FCSTD DOCUMENT  (FreeCAD 0.22R38314 (Git))
Label: myFile.groovy
License: All rights reserved
LicenseURL: https://en.wikipedia.org/wiki/All_rights_reserved
objects: Part::Feature×4, PartDesign::Plane×4, Sketcher::SketchObject×4, Mesh::Feature×2, PartDesign::Body×1
note: 13 computed .brp shape members not serialized (recipe doc carries the construction recipe); baked Part::Feature solids carry a one-line shape summary decoded from their .brp

FEATURE [Part::Feature] ReferenceFrame
  Placement = pos=(30,0,0) rot=(0,-1,0;1.57076rad)
FEATURE [PartDesign::Plane] DatumPlane_upperArm_1
  Length = 20
  Placement = pos=(30,0,0) rot=(0,-1,0;1.57076rad)
  ResizeMode = 0
  Width = 20
FEATURE [Sketcher::SketchObject] SVGSketch_upperArm_1
  FullyConstrained = false
  Placement = pos=(30,0,0) rot=(0,-1,0;1.57076rad)
  sketch-geometry (137):
    g0: LineSegment StartX=2.496 StartY=2.988 StartZ=0 EndX=2.388 EndY=2.988 EndZ=0
    g1: LineSegment StartX=2.388 StartY=2.988 StartZ=0 EndX=2.28 EndY=2.964 EndZ=0
    g2: LineSegment StartX=2.28 StartY=2.964 StartZ=0 EndX=2.172 EndY=2.952 EndZ=0
    g3: LineSegment StartX=2.172 StartY=2.952 StartZ=0 EndX=2.064 EndY=2.922 EndZ=0
    g4: LineSegment StartX=2.064 StartY=2.922 StartZ=0 EndX=1.962 EndY=2.892 EndZ=0
    g5: LineSegment StartX=1.962 StartY=2.892 StartZ=0 EndX=1.86 EndY=2.85 EndZ=0
    g6: LineSegment StartX=1.86 StartY=2.85 StartZ=0 EndX=1.764 EndY=2.808 EndZ=0
    g7: LineSegment StartX=1.764 StartY=2.808 StartZ=0 EndX=1.662 EndY=2.754 EndZ=0
    g8: LineSegment StartX=1.662 StartY=2.754 StartZ=0 EndX=1.59 EndY=2.718 EndZ=0
    g9: LineSegment StartX=1.59 StartY=2.718 StartZ=0 EndX=1.5 EndY=2.658 EndZ=0
    g10: LineSegment StartX=1.5 StartY=2.658 StartZ=0 EndX=1.392 EndY=2.586 EndZ=0
    g11: LineSegment StartX=1.392 StartY=2.586 StartZ=0 EndX=1.308 EndY=2.514 EndZ=0
    g12: LineSegment StartX=1.308 StartY=2.514 StartZ=0 EndX=1.224 EndY=2.442 EndZ=0
    g13: LineSegment StartX=1.224 StartY=2.442 StartZ=0 EndX=1.152 EndY=2.364 EndZ=0
    g14: LineSegment StartX=1.152 StartY=2.364 StartZ=0 EndX=1.074 EndY=2.28 EndZ=0
    g15: LineSegment StartX=1.074 StartY=2.28 StartZ=0 EndX=0.96 EndY=2.142 EndZ=0
    g16: LineSegment StartX=0.96 StartY=2.142 StartZ=0 EndX=0.804 EndY=1.956 EndZ=0
    g17: LineSegment StartX=0.804 StartY=1.956 StartZ=0 EndX=0.762 EndY=1.908 EndZ=0
    g18: LineSegment StartX=0.762 StartY=1.908 StartZ=0 EndX=0.582 EndY=1.692 EndZ=0
    g19: LineSegment StartX=0.582 StartY=1.692 StartZ=0 EndX=0.468 EndY=1.56 EndZ=0
    g20: LineSegment StartX=0.468 StartY=1.56 StartZ=0 EndX=0.42 EndY=1.5 EndZ=0
    g21: LineSegment StartX=0.42 StartY=1.5 StartZ=0 EndX=0.234 EndY=1.278 EndZ=0
    g22: LineSegment StartX=0.234 StartY=1.278 StartZ=0 EndX=0.156 EndY=1.182 EndZ=0
    g23: LineSegment StartX=0.156 StartY=1.182 StartZ=0 EndX=0.138 EndY=1.164 EndZ=0
    g24: LineSegment StartX=0.138 StartY=1.164 StartZ=0 EndX=-3.6e-15 EndY=0.996 EndZ=0
    g25: LineSegment StartX=-3.6e-15 StartY=0.996 StartZ=0 EndX=-3.6e-15 EndY=0.018 EndZ=0
    g26: LineSegment StartX=-3.6e-15 StartY=0.018 StartZ=0 EndX=-3.6e-15 EndY=-1.002 EndZ=0
    g27: LineSegment StartX=-3.6e-15 StartY=-1.002 StartZ=0 EndX=0.09 EndY=-1.11 EndZ=0
    g28: LineSegment StartX=0.09 StartY=-1.11 StartZ=0 EndX=0.156 EndY=-1.194 EndZ=0
    g29: LineSegment StartX=0.156 StartY=-1.194 StartZ=0 EndX=0.234 EndY=-1.284 EndZ=0
    g30: LineSegment StartX=0.234 StartY=-1.284 StartZ=0 EndX=0.396 EndY=-1.482 EndZ=0
    g31: LineSegment StartX=0.396 StartY=-1.482 StartZ=0 EndX=0.582 EndY=-1.698 EndZ=0
    g32: LineSegment StartX=0.582 StartY=-1.698 StartZ=0 EndX=0.762 EndY=-1.914 EndZ=0
    g33: LineSegment StartX=0.762 StartY=-1.914 StartZ=0 EndX=0.804 EndY=-1.962 EndZ=0
    g34: LineSegment StartX=0.804 StartY=-1.962 StartZ=0 EndX=0.96 EndY=-2.154 EndZ=0
    g35: LineSegment StartX=0.96 StartY=-2.154 StartZ=0 EndX=1.074 EndY=-2.286 EndZ=0
    g36: LineSegment StartX=1.074 StartY=-2.286 StartZ=0 EndX=1.152 EndY=-2.37 EndZ=0
    g37: LineSegment StartX=1.152 StartY=-2.37 StartZ=0 EndX=1.224 EndY=-2.448 EndZ=0
    g38: LineSegment StartX=1.224 StartY=-2.448 StartZ=0 EndX=1.308 EndY=-2.52 EndZ=0
    g39: LineSegment StartX=1.308 StartY=-2.52 StartZ=0 EndX=1.38 EndY=-2.58 EndZ=0
    g40: LineSegment StartX=1.38 StartY=-2.58 StartZ=0 EndX=1.5 EndY=-2.664 EndZ=0
    g41: LineSegment StartX=1.5 StartY=-2.664 StartZ=0 EndX=1.59 EndY=-2.724 EndZ=0
    g42: LineSegment StartX=1.59 StartY=-2.724 StartZ=0 EndX=1.662 EndY=-2.76 EndZ=0
    g43: LineSegment StartX=1.662 StartY=-2.76 StartZ=0 EndX=1.764 EndY=-2.814 EndZ=0
    g44: LineSegment StartX=1.764 StartY=-2.814 StartZ=0 EndX=1.86 EndY=-2.856 EndZ=0
    g45: LineSegment StartX=1.86 StartY=-2.856 StartZ=0 EndX=1.962 EndY=-2.898 EndZ=0
    g46: LineSegment StartX=1.962 StartY=-2.898 StartZ=0 EndX=2.064 EndY=-2.928 EndZ=0
    g47: LineSegment StartX=2.064 StartY=-2.928 StartZ=0 EndX=2.172 EndY=-2.958 EndZ=0
    g48: LineSegment StartX=2.172 StartY=-2.958 StartZ=0 EndX=2.28 EndY=-2.97 EndZ=0
    g49: LineSegment StartX=2.28 StartY=-2.97 StartZ=0 EndX=2.388 EndY=-2.994 EndZ=0
    g50: LineSegment StartX=2.388 StartY=-2.994 StartZ=0 EndX=2.496 EndY=-2.994 EndZ=0
    g51: LineSegment StartX=2.496 StartY=-2.994 StartZ=0 EndX=2.61 EndY=-3 EndZ=0
    g52: LineSegment StartX=2.61 StartY=-3 StartZ=0 EndX=2.796 EndY=-3 EndZ=0
    g53: LineSegment StartX=2.796 StartY=-3 StartZ=0 EndX=3 EndY=-3 EndZ=0
    g54: LineSegment StartX=3 StartY=-3 StartZ=0 EndX=3.15 EndY=-2.994 EndZ=0
    g55: LineSegment StartX=3.15 StartY=-2.994 StartZ=0 EndX=3.294 EndY=-2.988 EndZ=0
    g56: LineSegment StartX=3.294 StartY=-2.988 StartZ=0 EndX=3.444 EndY=-2.964 EndZ=0
    g57: LineSegment StartX=3.444 StartY=-2.964 StartZ=0 EndX=3.582 EndY=-2.946 EndZ=0
    g58: LineSegment StartX=3.582 StartY=-2.946 StartZ=0 EndX=3.726 EndY=-2.91 EndZ=0
    g59: LineSegment StartX=3.726 StartY=-2.91 StartZ=0 EndX=3.87 EndY=-2.874 EndZ=0
    g60: LineSegment StartX=3.87 StartY=-2.874 StartZ=0 EndX=4.008 EndY=-2.82 EndZ=0
    g61: LineSegment StartX=4.008 StartY=-2.82 StartZ=0 EndX=4.146 EndY=-2.772 EndZ=0
    g62: LineSegment StartX=4.146 StartY=-2.772 StartZ=0 EndX=4.284 EndY=-2.712 EndZ=0
    g63: LineSegment StartX=4.284 StartY=-2.712 StartZ=0 EndX=4.32 EndY=-2.694 EndZ=0
    g64: LineSegment StartX=4.32 StartY=-2.694 StartZ=0 EndX=4.446 EndY=-2.616 EndZ=0
    g65: LineSegment StartX=4.446 StartY=-2.616 StartZ=0 EndX=4.56 EndY=-2.562 EndZ=0
    g66: LineSegment StartX=4.56 StartY=-2.562 StartZ=0 EndX=4.662 EndY=-2.496 EndZ=0
    g67: LineSegment StartX=4.662 StartY=-2.496 StartZ=0 EndX=4.758 EndY=-2.43 EndZ=0
    g68: LineSegment StartX=4.758 StartY=-2.43 StartZ=0 EndX=4.854 EndY=-2.34 EndZ=0
    g69: LineSegment StartX=4.854 StartY=-2.34 StartZ=0 EndX=4.938 EndY=-2.28 EndZ=0
    g70: LineSegment StartX=4.938 StartY=-2.28 StartZ=0 EndX=4.974 EndY=-2.256 EndZ=0
    g71: LineSegment StartX=4.974 StartY=-2.256 StartZ=0 EndX=5.01 EndY=-2.22 EndZ=0
    g72: LineSegment StartX=5.01 StartY=-2.22 StartZ=0 EndX=5.118 EndY=-2.124 EndZ=0
    g73: LineSegment StartX=5.118 StartY=-2.124 StartZ=0 EndX=5.22 EndY=-2.016 EndZ=0
    g74: LineSegment StartX=5.22 StartY=-2.016 StartZ=0 EndX=5.31 EndY=-1.89 EndZ=0
    g75: LineSegment StartX=5.31 StartY=-1.89 StartZ=0 EndX=5.364 EndY=-1.836 EndZ=0
    g76: LineSegment StartX=5.364 StartY=-1.836 StartZ=0 EndX=5.49 EndY=-1.668 EndZ=0
    g77: LineSegment StartX=5.49 StartY=-1.668 StartZ=0 EndX=5.556 EndY=-1.566 EndZ=0
    g78: LineSegment StartX=5.556 StartY=-1.566 StartZ=0 EndX=5.61 EndY=-1.452 EndZ=0
    g79: LineSegment StartX=5.61 StartY=-1.452 StartZ=0 EndX=5.706 EndY=-1.284 EndZ=0
    g80: LineSegment StartX=5.706 StartY=-1.284 StartZ=0 EndX=5.754 EndY=-1.188 EndZ=0
    g81: LineSegment StartX=5.754 StartY=-1.188 StartZ=0 EndX=5.766 EndY=-1.152 EndZ=0
    g82: LineSegment StartX=5.766 StartY=-1.152 StartZ=0 EndX=5.778 EndY=-1.116 EndZ=0
    g83: LineSegment StartX=5.778 StartY=-1.116 StartZ=0 EndX=5.82 EndY=-1.014 EndZ=0
    g84: LineSegment StartX=5.82 StartY=-1.014 StartZ=0 EndX=5.868 EndY=-0.876 EndZ=0
    g85: LineSegment StartX=5.868 StartY=-0.876 StartZ=0 EndX=5.88 EndY=-0.834 EndZ=0
    g86: LineSegment StartX=5.88 StartY=-0.834 StartZ=0 EndX=5.898 EndY=-0.726 EndZ=0
    g87: LineSegment StartX=5.898 StartY=-0.726 StartZ=0 EndX=5.934 EndY=-0.588 EndZ=0
    g88: LineSegment StartX=5.934 StartY=-0.588 StartZ=0 EndX=5.952 EndY=-0.516 EndZ=0
    g89: LineSegment StartX=5.952 StartY=-0.516 StartZ=0 EndX=5.952 EndY=-0.486 EndZ=0
    g90: LineSegment StartX=5.952 StartY=-0.486 StartZ=0 EndX=5.964 EndY=-0.402 EndZ=0
    g91: LineSegment StartX=5.964 StartY=-0.402 StartZ=0 EndX=5.97 EndY=-0.288 EndZ=0
    g92: LineSegment StartX=5.97 StartY=-0.288 StartZ=0 EndX=5.982 EndY=-0.204 EndZ=0
    g93: LineSegment StartX=5.982 StartY=-0.204 StartZ=0 EndX=5.994 EndY=-0.006 EndZ=0
    g94: LineSegment StartX=5.994 StartY=-0.006 StartZ=0 EndX=5.994 EndY=0.114 EndZ=0
    g95: LineSegment StartX=5.994 StartY=0.114 StartZ=0 EndX=5.976 EndY=0.312 EndZ=0
    g96: LineSegment StartX=5.976 StartY=0.312 StartZ=0 EndX=5.964 EndY=0.426 EndZ=0
    g97: LineSegment StartX=5.964 StartY=0.426 StartZ=0 EndX=5.952 EndY=0.498 EndZ=0
    g98: LineSegment StartX=5.952 StartY=0.498 StartZ=0 EndX=5.94 EndY=0.582 EndZ=0
    g99: LineSegment StartX=5.94 StartY=0.582 StartZ=0 EndX=5.904 EndY=0.726 EndZ=0
    g100: LineSegment StartX=5.904 StartY=0.726 StartZ=0 EndX=5.868 EndY=0.87 EndZ=0
    g101: LineSegment StartX=5.868 StartY=0.87 StartZ=0 EndX=5.82 EndY=1.008 EndZ=0
    g102: LineSegment StartX=5.82 StartY=1.008 StartZ=0 EndX=5.766 EndY=1.146 EndZ=0
    g103: LineSegment StartX=5.766 StartY=1.146 StartZ=0 EndX=5.748 EndY=1.182 EndZ=0
    g104: LineSegment StartX=5.748 StartY=1.182 StartZ=0 EndX=5.706 EndY=1.278 EndZ=0
    g105: LineSegment StartX=5.706 StartY=1.278 StartZ=0 EndX=5.652 EndY=1.392 EndZ=0
    g106: LineSegment StartX=5.652 StartY=1.392 StartZ=0 EndX=5.64 EndY=1.416 EndZ=0
    g107: LineSegment StartX=5.64 StartY=1.416 StartZ=0 EndX=5.556 EndY=1.56 EndZ=0
    g108: LineSegment StartX=5.556 StartY=1.56 StartZ=0 EndX=5.49 EndY=1.662 EndZ=0
    g109: LineSegment StartX=5.49 StartY=1.662 StartZ=0 EndX=5.4 EndY=1.782 EndZ=0
    g110: LineSegment StartX=5.4 StartY=1.782 StartZ=0 EndX=5.274 EndY=1.95 EndZ=0
    g111: LineSegment StartX=5.274 StartY=1.95 StartZ=0 EndX=5.166 EndY=2.064 EndZ=0
    g112: LineSegment StartX=5.166 StartY=2.064 StartZ=0 EndX=5.112 EndY=2.112 EndZ=0
    g113: LineSegment StartX=5.112 StartY=2.112 StartZ=0 EndX=5.01 EndY=2.214 EndZ=0
    g114: LineSegment StartX=5.01 StartY=2.214 StartZ=0 EndX=4.974 EndY=2.25 EndZ=0
    g115: LineSegment StartX=4.974 StartY=2.25 StartZ=0 EndX=4.956 EndY=2.262 EndZ=0
    g116: LineSegment StartX=4.956 StartY=2.262 StartZ=0 EndX=4.86 EndY=2.334 EndZ=0
    g117: LineSegment StartX=4.86 StartY=2.334 StartZ=0 EndX=4.764 EndY=2.418 EndZ=0
    g118: LineSegment StartX=4.764 StartY=2.418 StartZ=0 EndX=4.662 EndY=2.49 EndZ=0
    g119: LineSegment StartX=4.662 StartY=2.49 StartZ=0 EndX=4.596 EndY=2.532 EndZ=0
    g120: LineSegment StartX=4.596 StartY=2.532 StartZ=0 EndX=4.536 EndY=2.568 EndZ=0
    g121: LineSegment StartX=4.536 StartY=2.568 StartZ=0 EndX=4.47 EndY=2.61 EndZ=0
    g122: LineSegment StartX=4.47 StartY=2.61 StartZ=0 EndX=4.434 EndY=2.634 EndZ=0
    g123: LineSegment StartX=4.434 StartY=2.634 StartZ=0 EndX=4.296 EndY=2.694 EndZ=0
    g124: LineSegment StartX=4.296 StartY=2.694 StartZ=0 EndX=4.188 EndY=2.748 EndZ=0
    g125: LineSegment StartX=4.188 StartY=2.748 StartZ=0 EndX=4.146 EndY=2.766 EndZ=0
    g126: LineSegment StartX=4.146 StartY=2.766 StartZ=0 EndX=4.008 EndY=2.814 EndZ=0
    g127: LineSegment StartX=4.008 StartY=2.814 StartZ=0 EndX=3.87 EndY=2.868 EndZ=0
    g128: LineSegment StartX=3.87 StartY=2.868 StartZ=0 EndX=3.732 EndY=2.904 EndZ=0
    g129: LineSegment StartX=3.732 StartY=2.904 StartZ=0 EndX=3.582 EndY=2.94 EndZ=0
    g130: LineSegment StartX=3.582 StartY=2.94 StartZ=0 EndX=3.444 EndY=2.958 EndZ=0
    g131: LineSegment StartX=3.444 StartY=2.958 StartZ=0 EndX=3.294 EndY=2.982 EndZ=0
    g132: LineSegment StartX=3.294 StartY=2.982 StartZ=0 EndX=3.15 EndY=2.988 EndZ=0
    g133: LineSegment StartX=3.15 StartY=2.988 StartZ=0 EndX=3 EndY=2.994 EndZ=0
    g134: LineSegment StartX=3 StartY=2.994 StartZ=0 EndX=2.808 EndY=2.994 EndZ=0
    g135: LineSegment StartX=2.808 StartY=2.994 StartZ=0 EndX=2.61 EndY=2.994 EndZ=0
    g136: LineSegment StartX=2.61 StartY=2.994 StartZ=0 EndX=2.496 EndY=2.988 EndZ=0
FEATURE [Part::Feature] ReferenceFrame001
  Placement = pos=(0,0,10) rot=(0,0,1;0rad)
FEATURE [PartDesign::Plane] DatumPlane_upperArm_2
  Length = 20
  Placement = pos=(0,0,10) rot=(0,0,1;0rad)
  ResizeMode = 0
  Width = 20
FEATURE [Sketcher::SketchObject] SVGSketch_upperArm_2
  FullyConstrained = false
  Placement = pos=(0,0,10) rot=(0,0,1;0rad)
  sketch-geometry (393):
    g0: LineSegment StartX=-0.797549 StartY=4.74985 StartZ=0 EndX=-0.697549 EndY=4.41652 EndZ=0
    g1: LineSegment StartX=-0.697549 StartY=4.41652 StartZ=0 EndX=-0.497549 EndY=4.18319 EndZ=0
    g2: LineSegment StartX=-0.497549 StartY=4.18319 StartZ=0 EndX=-0.197549 EndY=4.04985 EndZ=0
    g3: LineSegment StartX=-0.197549 StartY=4.04985 StartZ=0 EndX=-0.0308823 EndY=4.01652 EndZ=0
    g4: LineSegment StartX=-0.0308823 StartY=4.01652 StartZ=0 EndX=0.135784 EndY=4.04985 EndZ=0
    g5: LineSegment StartX=0.135784 StartY=4.04985 StartZ=0 EndX=0.469118 EndY=4.18319 EndZ=0
    g6: LineSegment StartX=0.469118 StartY=4.18319 StartZ=0 EndX=0.669118 EndY=4.41652 EndZ=0
    g7: LineSegment StartX=0.669118 StartY=4.41652 StartZ=0 EndX=0.769118 EndY=4.74985 EndZ=0
    g8: LineSegment StartX=0.769118 StartY=4.74985 StartZ=0 EndX=0.735784 EndY=5.08319 EndZ=0
    g9: LineSegment StartX=0.735784 StartY=5.08319 StartZ=0 EndX=0.569118 EndY=5.34985 EndZ=0
    g10: LineSegment StartX=0.569118 StartY=5.34985 StartZ=0 EndX=0.302451 EndY=5.54985 EndZ=0
    g11: LineSegment StartX=0.302451 StartY=5.54985 StartZ=0 EndX=-0.0308823 EndY=5.61652 EndZ=0
    g12: LineSegment StartX=-0.0308823 StartY=5.61652 StartZ=0 EndX=-0.330882 EndY=5.54985 EndZ=0
    g13: LineSegment StartX=-0.330882 StartY=5.54985 StartZ=0 EndX=-0.597549 EndY=5.34985 EndZ=0
    g14: LineSegment StartX=-0.597549 StartY=5.34985 StartZ=0 EndX=-0.764216 EndY=5.04985 EndZ=0
    g15: LineSegment StartX=-0.764216 StartY=5.04985 StartZ=0 EndX=-0.797549 EndY=4.74985 EndZ=0
    g16: LineSegment StartX=1.10245 StartY=2.21652 StartZ=0 EndX=0.802451 EndY=2.31652 EndZ=0
    g17: LineSegment StartX=0.802451 StartY=2.31652 StartZ=0 EndX=0.569118 EndY=2.41652 EndZ=0
    g18: LineSegment StartX=0.569118 StartY=2.41652 StartZ=0 EndX=-0.0642157 EndY=2.48319 EndZ=0
    g19: LineSegment StartX=-0.0642157 StartY=2.48319 StartZ=0 EndX=-0.597549 EndY=2.41652 EndZ=0
    g20: LineSegment StartX=-0.597549 StartY=2.41652 StartZ=0 EndX=-0.830882 EndY=2.31652 EndZ=0
    g21: LineSegment StartX=-0.830882 StartY=2.31652 StartZ=0 EndX=-1.13088 EndY=2.21652 EndZ=0
    g22: LineSegment StartX=-1.13088 StartY=2.21652 StartZ=0 EndX=-1.63088 EndY=1.88319 EndZ=0
    g23: LineSegment StartX=-1.63088 StartY=1.88319 StartZ=0 EndX=-2.03088 EndY=1.48319 EndZ=0
    g24: LineSegment StartX=-2.03088 StartY=1.48319 StartZ=0 EndX=-2.09755 EndY=1.34985 EndZ=0
    g25: LineSegment StartX=-2.09755 StartY=1.34985 StartZ=0 EndX=-2.29755 EndY=0.983187 EndZ=0
    g26: LineSegment StartX=-2.29755 StartY=0.983187 StartZ=0 EndX=-2.46422 EndY=0.41652 EndZ=0
    g27: LineSegment StartX=-2.46422 StartY=0.41652 StartZ=0 EndX=-2.49755 EndY=-0.150146 EndZ=0
    g28: LineSegment StartX=-2.49755 StartY=-0.150146 StartZ=0 EndX=-2.36422 EndY=-0.816813 EndZ=0
    g29: LineSegment StartX=-2.36422 StartY=-0.816813 StartZ=0 EndX=-2.19755 EndY=-1.25015 EndZ=0
    g30: LineSegment StartX=-2.19755 StartY=-1.25015 StartZ=0 EndX=-1.83088 EndY=-1.71681 EndZ=0
    g31: LineSegment StartX=-1.83088 StartY=-1.71681 StartZ=0 EndX=-1.39755 EndY=-2.11681 EndZ=0
    g32: LineSegment StartX=-1.39755 StartY=-2.11681 StartZ=0 EndX=-1.13088 EndY=-2.25015 EndZ=0
    g33: LineSegment StartX=-1.13088 StartY=-2.25015 StartZ=0 EndX=-0.830882 EndY=-2.38348 EndZ=0
    g34: LineSegment StartX=-0.830882 StartY=-2.38348 StartZ=0 EndX=-0.297549 EndY=-2.48348 EndZ=0
    g35: LineSegment StartX=-0.297549 StartY=-2.48348 StartZ=0 EndX=-0.164216 EndY=-2.51681 EndZ=0
    g36: LineSegment StartX=-0.164216 StartY=-2.51681 StartZ=0 EndX=-0.0308823 EndY=-2.51681 EndZ=0
    g37: LineSegment StartX=-0.0308823 StartY=-2.51681 StartZ=0 EndX=0.269118 EndY=-2.48348 EndZ=0
    g38: LineSegment StartX=0.269118 StartY=-2.48348 StartZ=0 EndX=0.835784 EndY=-2.35015 EndZ=0
    g39: LineSegment StartX=0.835784 StartY=-2.35015 StartZ=0 EndX=1.40245 EndY=-2.08348 EndZ=0
    g40: LineSegment StartX=1.40245 StartY=-2.08348 StartZ=0 EndX=1.56912 EndY=-1.91681 EndZ=0
    g41: LineSegment StartX=1.56912 StartY=-1.91681 StartZ=0 EndX=1.80245 EndY=-1.71681 EndZ=0
    g42: LineSegment StartX=1.80245 StartY=-1.71681 StartZ=0 EndX=2.13578 EndY=-1.25015 EndZ=0
    g43: LineSegment StartX=2.13578 StartY=-1.25015 StartZ=0 EndX=2.36912 EndY=-0.750146 EndZ=0
    g44: LineSegment StartX=2.36912 StartY=-0.750146 StartZ=0 EndX=2.46912 EndY=-0.150146 EndZ=0
    g45: LineSegment StartX=2.46912 StartY=-0.150146 StartZ=0 EndX=2.43578 EndY=0.41652 EndZ=0
    g46: LineSegment StartX=2.43578 StartY=0.41652 StartZ=0 EndX=2.26912 EndY=0.983187 EndZ=0
    g47: LineSegment StartX=2.26912 StartY=0.983187 StartZ=0 EndX=2.06912 EndY=1.34985 EndZ=0
    g48: LineSegment StartX=2.06912 StartY=1.34985 StartZ=0 EndX=2.00245 EndY=1.48319 EndZ=0
    g49: LineSegment StartX=2.00245 StartY=1.48319 StartZ=0 EndX=1.56912 EndY=1.91652 EndZ=0
    g50: LineSegment StartX=1.56912 StartY=1.91652 StartZ=0 EndX=1.10245 EndY=2.21652 EndZ=0
    g51: LineSegment StartX=61.8358 StartY=-2.38348 StartZ=0 EndX=61.6691 EndY=-2.31681 EndZ=0
    g52: LineSegment StartX=61.6691 StartY=-2.31681 StartZ=0 EndX=61.4691 EndY=-2.28348 EndZ=0
    g53: LineSegment StartX=61.4691 StartY=-2.28348 StartZ=0 EndX=61.1358 EndY=-2.35015 EndZ=0
    g54: LineSegment StartX=61.1358 StartY=-2.35015 StartZ=0 EndX=60.8691 EndY=-2.55015 EndZ=0
    g55: LineSegment StartX=60.8691 StartY=-2.55015 StartZ=0 EndX=60.7025 EndY=-2.85015 EndZ=0
    g56: LineSegment StartX=60.7025 StartY=-2.85015 StartZ=0 EndX=60.7025 EndY=-2.98348 EndZ=0
    g57: LineSegment StartX=60.7025 StartY=-2.98348 StartZ=0 EndX=60.6691 EndY=-3.08348 EndZ=0
    g58: LineSegment StartX=60.6691 StartY=-3.08348 StartZ=0 EndX=60.6691 EndY=-3.18348 EndZ=0
    g59: LineSegment StartX=60.6691 StartY=-3.18348 StartZ=0 EndX=60.7691 EndY=-3.48348 EndZ=0
    g60: LineSegment StartX=60.7691 StartY=-3.48348 StartZ=0 EndX=61.0025 EndY=-3.75015 EndZ=0
    g61: LineSegment StartX=61.0025 StartY=-3.75015 StartZ=0 EndX=61.3025 EndY=-3.88348 EndZ=0
    g62: LineSegment StartX=61.3025 StartY=-3.88348 StartZ=0 EndX=61.5358 EndY=-3.88348 EndZ=0
    g63: LineSegment StartX=61.5358 StartY=-3.88348 StartZ=0 EndX=61.6358 EndY=-3.88348 EndZ=0
    g64: LineSegment StartX=61.6358 StartY=-3.88348 StartZ=0 EndX=61.9358 EndY=-3.75015 EndZ=0
    g65: LineSegment StartX=61.9358 StartY=-3.75015 StartZ=0 EndX=62.1691 EndY=-3.48348 EndZ=0
    g66: LineSegment StartX=62.1691 StartY=-3.48348 StartZ=0 EndX=62.2025 EndY=-3.31681 EndZ=0
    g67: LineSegment StartX=62.2025 StartY=-3.31681 StartZ=0 EndX=62.2691 EndY=-3.18348 EndZ=0
    g68: LineSegment StartX=62.2691 StartY=-3.18348 StartZ=0 EndX=62.2358 EndY=-2.85015 EndZ=0
    g69: LineSegment StartX=62.2358 StartY=-2.85015 StartZ=0 EndX=62.1691 EndY=-2.75015 EndZ=0
    g70: LineSegment StartX=62.1691 StartY=-2.75015 StartZ=0 EndX=62.1358 EndY=-2.65015 EndZ=0
    g71: LineSegment StartX=62.1358 StartY=-2.65015 StartZ=0 EndX=62.0691 EndY=-2.55015 EndZ=0
    g72: LineSegment StartX=62.0691 StartY=-2.55015 StartZ=0 EndX=61.9691 EndY=-2.48348 EndZ=0
    g73: LineSegment StartX=61.9691 StartY=-2.48348 StartZ=0 EndX=61.8358 EndY=-2.38348 EndZ=0
    g74: LineSegment StartX=58.8025 StartY=0.91652 StartZ=0 EndX=58.6691 EndY=0.683187 EndZ=0
    g75: LineSegment StartX=58.6691 StartY=0.683187 StartZ=0 EndX=58.6025 EndY=0.51652 EndZ=0
    g76: LineSegment StartX=58.6025 StartY=0.51652 StartZ=0 EndX=58.5025 EndY=0.083187 EndZ=0
    g77: LineSegment StartX=58.5025 StartY=0.083187 StartZ=0 EndX=58.5358 EndY=-0.350146 EndZ=0
    g78: LineSegment StartX=58.5358 StartY=-0.350146 StartZ=0 EndX=58.6691 EndY=-0.750146 EndZ=0
    g79: LineSegment StartX=58.6691 StartY=-0.750146 StartZ=0 EndX=58.8358 EndY=-0.950146 EndZ=0
    g80: LineSegment StartX=58.8358 StartY=-0.950146 StartZ=0 EndX=58.9691 EndY=-1.11681 EndZ=0
    g81: LineSegment StartX=58.9691 StartY=-1.11681 StartZ=0 EndX=59.3358 EndY=-1.38348 EndZ=0
    g82: LineSegment StartX=59.3358 StartY=-1.38348 StartZ=0 EndX=59.7691 EndY=-1.48348 EndZ=0
    g83: LineSegment StartX=59.7691 StartY=-1.48348 StartZ=0 EndX=59.9691 EndY=-1.51681 EndZ=0
    g84: LineSegment StartX=59.9691 StartY=-1.51681 StartZ=0 EndX=60.2025 EndY=-1.48348 EndZ=0
    g85: LineSegment StartX=60.2025 StartY=-1.48348 StartZ=0 EndX=60.6358 EndY=-1.38348 EndZ=0
    g86: LineSegment StartX=60.6358 StartY=-1.38348 StartZ=0 EndX=61.0025 EndY=-1.11681 EndZ=0
    g87: LineSegment StartX=61.0025 StartY=-1.11681 StartZ=0 EndX=61.2691 EndY=-0.750146 EndZ=0
    g88: LineSegment StartX=61.2691 StartY=-0.750146 StartZ=0 EndX=61.4358 EndY=-0.350146 EndZ=0
    g89: LineSegment StartX=61.4358 StartY=-0.350146 StartZ=0 EndX=61.4691 EndY=0.083187 EndZ=0
    g90: LineSegment StartX=61.4691 StartY=0.083187 StartZ=0 EndX=61.3691 EndY=0.51652 EndZ=0
    g91: LineSegment StartX=61.3691 StartY=0.51652 StartZ=0 EndX=61.3025 EndY=0.683187 EndZ=0
    g92: LineSegment StartX=61.3025 StartY=0.683187 StartZ=0 EndX=61.1691 EndY=0.91652 EndZ=0
    g93: LineSegment StartX=61.1691 StartY=0.91652 StartZ=0 EndX=60.8358 EndY=1.21652 EndZ=0
    g94: LineSegment StartX=60.8358 StartY=1.21652 StartZ=0 EndX=60.4358 EndY=1.41652 EndZ=0
    g95: LineSegment StartX=60.4358 StartY=1.41652 StartZ=0 EndX=59.9691 EndY=1.48319 EndZ=0
    g96: LineSegment StartX=59.9691 StartY=1.48319 StartZ=0 EndX=59.5358 EndY=1.41652 EndZ=0
    g97: LineSegment StartX=59.5358 StartY=1.41652 StartZ=0 EndX=59.1358 EndY=1.21652 EndZ=0
    g98: LineSegment StartX=59.1358 StartY=1.21652 StartZ=0 EndX=58.8025 EndY=0.91652 EndZ=0
    g99: LineSegment StartX=60.4691 StartY=2.74985 StartZ=0 EndX=60.6691 EndY=2.98319 EndZ=0
    g100: LineSegment StartX=60.6691 StartY=2.98319 StartZ=0 EndX=60.7691 EndY=3.24985 EndZ=0
    g101: LineSegment StartX=60.7691 StartY=3.24985 StartZ=0 EndX=60.7358 EndY=3.38319 EndZ=0
    g102: LineSegment StartX=60.7358 StartY=3.38319 StartZ=0 EndX=60.7691 EndY=3.54985 EndZ=0
    g103: LineSegment StartX=60.7691 StartY=3.54985 StartZ=0 EndX=60.7358 EndY=3.64985 EndZ=0
    g104: LineSegment StartX=60.7358 StartY=3.64985 StartZ=0 EndX=60.6358 EndY=3.84985 EndZ=0
    g105: LineSegment StartX=60.6358 StartY=3.84985 StartZ=0 EndX=60.5691 EndY=3.94985 EndZ=0
    g106: LineSegment StartX=60.5691 StartY=3.94985 StartZ=0 EndX=60.3025 EndY=4.11652 EndZ=0
    g107: LineSegment StartX=60.3025 StartY=4.11652 StartZ=0 EndX=59.9691 EndY=4.18319 EndZ=0
    g108: LineSegment StartX=59.9691 StartY=4.18319 StartZ=0 EndX=59.6691 EndY=4.11652 EndZ=0
    g109: LineSegment StartX=59.6691 StartY=4.11652 StartZ=0 EndX=59.4025 EndY=3.91652 EndZ=0
    g110: LineSegment StartX=59.4025 StartY=3.91652 StartZ=0 EndX=59.2358 EndY=3.64985 EndZ=0
    g111: LineSegment StartX=59.2358 StartY=3.64985 StartZ=0 EndX=59.2025 EndY=3.54985 EndZ=0
    g112: LineSegment StartX=59.2025 StartY=3.54985 StartZ=0 EndX=59.2025 EndY=3.41652 EndZ=0
    g113: LineSegment StartX=59.2025 StartY=3.41652 StartZ=0 EndX=59.2025 EndY=3.28319 EndZ=0
    g114: LineSegment StartX=59.2025 StartY=3.28319 StartZ=0 EndX=59.2691 EndY=3.08319 EndZ=0
    g115: LineSegment StartX=59.2691 StartY=3.08319 StartZ=0 EndX=59.3025 EndY=2.98319 EndZ=0
    g116: LineSegment StartX=59.3025 StartY=2.98319 StartZ=0 EndX=59.5025 EndY=2.74985 EndZ=0
    g117: LineSegment StartX=59.5025 StartY=2.74985 StartZ=0 EndX=59.8025 EndY=2.61652 EndZ=0
    g118: LineSegment StartX=59.8025 StartY=2.61652 StartZ=0 EndX=59.9691 EndY=2.58319 EndZ=0
    g119: LineSegment StartX=59.9691 StartY=2.58319 StartZ=0 EndX=60.1691 EndY=2.61652 EndZ=0
    g120: LineSegment StartX=60.1691 StartY=2.61652 StartZ=0 EndX=60.4691 EndY=2.74985 EndZ=0
    g121: LineSegment StartX=59.2358 StartY=-3.38348 StartZ=0 EndX=59.3025 EndY=-3.11681 EndZ=0
    g122: LineSegment StartX=59.3025 StartY=-3.11681 StartZ=0 EndX=59.2691 EndY=-2.98348 EndZ=0
    g123: LineSegment StartX=59.2691 StartY=-2.98348 StartZ=0 EndX=59.2691 EndY=-2.85015 EndZ=0
    g124: LineSegment StartX=59.2691 StartY=-2.85015 StartZ=0 EndX=59.1025 EndY=-2.55015 EndZ=0
    g125: LineSegment StartX=59.1025 StartY=-2.55015 StartZ=0 EndX=58.8358 EndY=-2.35015 EndZ=0
    g126: LineSegment StartX=58.8358 StartY=-2.35015 StartZ=0 EndX=58.5025 EndY=-2.28348 EndZ=0
    g127: LineSegment StartX=58.5025 StartY=-2.28348 StartZ=0 EndX=58.1691 EndY=-2.35015 EndZ=0
    g128: LineSegment StartX=58.1691 StartY=-2.35015 StartZ=0 EndX=58.0691 EndY=-2.41681 EndZ=0
    g129: LineSegment StartX=58.0691 StartY=-2.41681 StartZ=0 EndX=57.9025 EndY=-2.55015 EndZ=0
    g130: LineSegment StartX=57.9025 StartY=-2.55015 StartZ=0 EndX=57.8025 EndY=-2.75015 EndZ=0
    g131: LineSegment StartX=57.8025 StartY=-2.75015 StartZ=0 EndX=57.7358 EndY=-2.85015 EndZ=0
    g132: LineSegment StartX=57.7358 StartY=-2.85015 StartZ=0 EndX=57.7025 EndY=-3.18348 EndZ=0
    g133: LineSegment StartX=57.7025 StartY=-3.18348 StartZ=0 EndX=57.7358 EndY=-3.28348 EndZ=0
    g134: LineSegment StartX=57.7358 StartY=-3.28348 StartZ=0 EndX=57.8025 EndY=-3.48348 EndZ=0
    g135: LineSegment StartX=57.8025 StartY=-3.48348 StartZ=0 EndX=58.0358 EndY=-3.75015 EndZ=0
    g136: LineSegment StartX=58.0358 StartY=-3.75015 StartZ=0 EndX=58.1358 EndY=-3.78348 EndZ=0
    g137: LineSegment StartX=58.1358 StartY=-3.78348 StartZ=0 EndX=58.3358 EndY=-3.88348 EndZ=0
    g138: LineSegment StartX=58.3358 StartY=-3.88348 StartZ=0 EndX=58.5025 EndY=-3.88348 EndZ=0
    g139: LineSegment StartX=58.5025 StartY=-3.88348 StartZ=0 EndX=58.6691 EndY=-3.88348 EndZ=0
    g140: LineSegment StartX=58.6691 StartY=-3.88348 StartZ=0 EndX=58.8358 EndY=-3.78348 EndZ=0
    g141: LineSegment StartX=58.8358 StartY=-3.78348 StartZ=0 EndX=58.9691 EndY=-3.75015 EndZ=0
    g142: LineSegment StartX=58.9691 StartY=-3.75015 StartZ=0 EndX=59.2025 EndY=-3.48348 EndZ=0
    g143: LineSegment StartX=59.2025 StartY=-3.48348 StartZ=0 EndX=59.2358 EndY=-3.38348 EndZ=0
    g144: LineSegment StartX=-3.36422 StartY=2.98319 StartZ=0 EndX=-3.13088 EndY=2.88319 EndZ=0
    g145: LineSegment StartX=-3.13088 StartY=2.88319 StartZ=0 EndX=-3.03088 EndY=2.91652 EndZ=0
    g146: LineSegment StartX=-3.03088 StartY=2.91652 StartZ=0 EndX=-2.89755 EndY=2.98319 EndZ=0
    g147: LineSegment StartX=-2.89755 StartY=2.98319 StartZ=0 EndX=-2.79755 EndY=2.98319 EndZ=0
    g148: LineSegment StartX=-2.79755 StartY=2.98319 StartZ=0 EndX=-2.66422 EndY=3.04985 EndZ=0
    g149: LineSegment StartX=-2.66422 StartY=3.04985 StartZ=0 EndX=-2.43088 EndY=3.31652 EndZ=0
    g150: LineSegment StartX=-2.43088 StartY=3.31652 StartZ=0 EndX=-2.33088 EndY=3.61652 EndZ=0
    g151: LineSegment StartX=-2.33088 StartY=3.61652 StartZ=0 EndX=-2.36422 EndY=3.94985 EndZ=0
    g152: LineSegment StartX=-2.36422 StartY=3.94985 StartZ=0 EndX=-2.53088 EndY=4.21652 EndZ=0
    g153: LineSegment StartX=-2.53088 StartY=4.21652 StartZ=0 EndX=-2.79755 EndY=4.41652 EndZ=0
    g154: LineSegment StartX=-2.79755 StartY=4.41652 StartZ=0 EndX=-2.96422 EndY=4.44985 EndZ=0
    g155: LineSegment StartX=-2.96422 StartY=4.44985 StartZ=0 EndX=-3.13088 EndY=4.48319 EndZ=0
    g156: LineSegment StartX=-3.13088 StartY=4.48319 StartZ=0 EndX=-3.46422 EndY=4.41652 EndZ=0
    g157: LineSegment StartX=-3.46422 StartY=4.41652 StartZ=0 EndX=-3.73088 EndY=4.21652 EndZ=0
    g158: LineSegment StartX=-3.73088 StartY=4.21652 StartZ=0 EndX=-3.89755 EndY=3.94985 EndZ=0
    g159: LineSegment StartX=-3.89755 StartY=3.94985 StartZ=0 EndX=-3.93088 EndY=3.61652 EndZ=0
    g160: LineSegment StartX=-3.93088 StartY=3.61652 StartZ=0 EndX=-3.83088 EndY=3.28319 EndZ=0
    g161: LineSegment StartX=-3.83088 StartY=3.28319 StartZ=0 EndX=-3.59755 EndY=3.04985 EndZ=0
    g162: LineSegment StartX=-3.59755 StartY=3.04985 StartZ=0 EndX=-3.46422 EndY=2.98319 EndZ=0
    g163: LineSegment StartX=-3.46422 StartY=2.98319 StartZ=0 EndX=-3.36422 EndY=2.98319 EndZ=0
    g164: LineSegment StartX=57.1691 StartY=1.31652 StartZ=0 EndX=57.2691 EndY=1.31652 EndZ=0
    g165: LineSegment StartX=57.2691 StartY=1.31652 StartZ=0 EndX=57.4691 EndY=1.31652 EndZ=0
    g166: LineSegment StartX=57.4691 StartY=1.31652 StartZ=0 EndX=57.5691 EndY=1.38319 EndZ=0
    g167: LineSegment StartX=57.5691 StartY=1.38319 StartZ=0 EndX=57.8025 EndY=1.44985 EndZ=0
    g168: LineSegment StartX=57.8025 StartY=1.44985 StartZ=0 EndX=58.0025 EndY=1.71652 EndZ=0
    g169: LineSegment StartX=58.0025 StartY=1.71652 StartZ=0 EndX=58.1025 EndY=2.04985 EndZ=0
    g170: LineSegment StartX=58.1025 StartY=2.04985 StartZ=0 EndX=58.0691 EndY=2.34985 EndZ=0
    g171: LineSegment StartX=58.0691 StartY=2.34985 StartZ=0 EndX=57.8691 EndY=2.68319 EndZ=0
    g172: LineSegment StartX=57.8691 StartY=2.68319 StartZ=0 EndX=57.7691 EndY=2.74985 EndZ=0
    g173: LineSegment StartX=57.7691 StartY=2.74985 StartZ=0 EndX=57.6358 EndY=2.84985 EndZ=0
    g174: LineSegment StartX=57.6358 StartY=2.84985 StartZ=0 EndX=57.4691 EndY=2.88319 EndZ=0
    g175: LineSegment StartX=57.4691 StartY=2.88319 StartZ=0 EndX=57.3025 EndY=2.91652 EndZ=0
    g176: LineSegment StartX=57.3025 StartY=2.91652 StartZ=0 EndX=57.1025 EndY=2.84985 EndZ=0
    g177: LineSegment StartX=57.1025 StartY=2.84985 StartZ=0 EndX=56.9691 EndY=2.81652 EndZ=0
    g178: LineSegment StartX=56.9691 StartY=2.81652 StartZ=0 EndX=56.7025 EndY=2.58319 EndZ=0
    g179: LineSegment StartX=56.7025 StartY=2.58319 StartZ=0 EndX=56.5691 EndY=2.34985 EndZ=0
    g180: LineSegment StartX=56.5691 StartY=2.34985 StartZ=0 EndX=56.5358 EndY=2.01652 EndZ=0
    g181: LineSegment StartX=56.5358 StartY=2.01652 StartZ=0 EndX=56.6358 EndY=1.71652 EndZ=0
    g182: LineSegment StartX=56.6358 StartY=1.71652 StartZ=0 EndX=56.8025 EndY=1.51652 EndZ=0
    g183: LineSegment StartX=56.8025 StartY=1.51652 StartZ=0 EndX=57.0025 EndY=1.38319 EndZ=0
    g184: LineSegment StartX=57.0025 StartY=1.38319 StartZ=0 EndX=57.1691 EndY=1.31652 EndZ=0
    g185: LineSegment StartX=-1.03088 StartY=-4.08348 StartZ=0 EndX=-1.26422 EndY=-3.88348 EndZ=0
    g186: LineSegment StartX=-1.26422 StartY=-3.88348 StartZ=0 EndX=-1.66422 EndY=-3.78348 EndZ=0
    g187: LineSegment StartX=-1.66422 StartY=-3.78348 StartZ=0 EndX=-1.99755 EndY=-3.85015 EndZ=0
    g188: LineSegment StartX=-1.99755 StartY=-3.85015 StartZ=0 EndX=-2.26422 EndY=-4.01681 EndZ=0
    g189: LineSegment StartX=-2.26422 StartY=-4.01681 StartZ=0 EndX=-2.43088 EndY=-4.31681 EndZ=0
    g190: LineSegment StartX=-2.43088 StartY=-4.31681 StartZ=0 EndX=-2.46422 EndY=-4.45015 EndZ=0
    g191: LineSegment StartX=-2.46422 StartY=-4.45015 StartZ=0 EndX=-2.46422 EndY=-4.65015 EndZ=0
    g192: LineSegment StartX=-2.46422 StartY=-4.65015 StartZ=0 EndX=-2.39755 EndY=-4.88348 EndZ=0
    g193: LineSegment StartX=-2.39755 StartY=-4.88348 StartZ=0 EndX=-2.36422 EndY=-4.98348 EndZ=0
    g194: LineSegment StartX=-2.36422 StartY=-4.98348 StartZ=0 EndX=-2.26422 EndY=-5.08348 EndZ=0
    g195: LineSegment StartX=-2.26422 StartY=-5.08348 StartZ=0 EndX=-2.13088 EndY=-5.21681 EndZ=0
    g196: LineSegment StartX=-2.13088 StartY=-5.21681 StartZ=0 EndX=-1.83088 EndY=-5.35015 EndZ=0
    g197: LineSegment StartX=-1.83088 StartY=-5.35015 StartZ=0 EndX=-1.66422 EndY=-5.35015 EndZ=0
    g198: LineSegment StartX=-1.66422 StartY=-5.35015 StartZ=0 EndX=-1.49755 EndY=-5.35015 EndZ=0
    g199: LineSegment StartX=-1.49755 StartY=-5.35015 StartZ=0 EndX=-1.19755 EndY=-5.21681 EndZ=0
    g200: LineSegment StartX=-1.19755 StartY=-5.21681 StartZ=0 EndX=-0.964216 EndY=-4.98348 EndZ=0
    g201: LineSegment StartX=-0.964216 StartY=-4.98348 StartZ=0 EndX=-0.864216 EndY=-4.65015 EndZ=0
    g202: LineSegment StartX=-0.864216 StartY=-4.65015 StartZ=0 EndX=-0.964216 EndY=-4.25015 EndZ=0
    g203: LineSegment StartX=-0.964216 StartY=-4.25015 StartZ=0 EndX=-1.03088 EndY=-4.08348 EndZ=0
    g204: LineSegment StartX=4.43578 StartY=1.54985 StartZ=0 EndX=4.16912 EndY=1.34985 EndZ=0
    g205: LineSegment StartX=4.16912 StartY=1.34985 StartZ=0 EndX=4.00245 EndY=1.08319 EndZ=0
    g206: LineSegment StartX=4.00245 StartY=1.08319 StartZ=0 EndX=3.96912 EndY=0.749854 EndZ=0
    g207: LineSegment StartX=3.96912 StartY=0.749854 StartZ=0 EndX=4.06912 EndY=0.41652 EndZ=0
    g208: LineSegment StartX=4.06912 StartY=0.41652 StartZ=0 EndX=4.26912 EndY=0.183187 EndZ=0
    g209: LineSegment StartX=4.26912 StartY=0.183187 StartZ=0 EndX=4.56912 EndY=0.0498537 EndZ=0
    g210: LineSegment StartX=4.56912 StartY=0.0498537 StartZ=0 EndX=4.80245 EndY=0.0165204 EndZ=0
    g211: LineSegment StartX=4.80245 StartY=0.0165204 StartZ=0 EndX=4.90245 EndY=0.0498537 EndZ=0
    g212: LineSegment StartX=4.90245 StartY=0.0498537 StartZ=0 EndX=5.23578 EndY=0.183187 EndZ=0
    g213: LineSegment StartX=5.23578 StartY=0.183187 StartZ=0 EndX=5.43578 EndY=0.41652 EndZ=0
    g214: LineSegment StartX=5.43578 StartY=0.41652 StartZ=0 EndX=5.50245 EndY=0.61652 EndZ=0
    g215: LineSegment StartX=5.50245 StartY=0.61652 StartZ=0 EndX=5.53578 EndY=0.749854 EndZ=0
    g216: LineSegment StartX=5.53578 StartY=0.749854 StartZ=0 EndX=5.50245 EndY=1.08319 EndZ=0
    g217: LineSegment StartX=5.50245 StartY=1.08319 StartZ=0 EndX=5.40245 EndY=1.21652 EndZ=0
    g218: LineSegment StartX=5.40245 StartY=1.21652 StartZ=0 EndX=5.33578 EndY=1.34985 EndZ=0
    g219: LineSegment StartX=5.33578 StartY=1.34985 StartZ=0 EndX=5.23578 EndY=1.44985 EndZ=0
    g220: LineSegment StartX=5.23578 StartY=1.44985 StartZ=0 EndX=5.06912 EndY=1.54985 EndZ=0
    g221: LineSegment StartX=5.06912 StartY=1.54985 StartZ=0 EndX=4.73578 EndY=1.61652 EndZ=0
    g222: LineSegment StartX=4.73578 StartY=1.61652 StartZ=0 EndX=4.43578 EndY=1.54985 EndZ=0
    g223: LineSegment StartX=-3.96422 StartY=-3.18348 StartZ=0 EndX=-3.73088 EndY=-3.08348 EndZ=0
    g224: LineSegment StartX=-3.73088 StartY=-3.08348 StartZ=0 EndX=-3.53088 EndY=-2.85015 EndZ=0
    g225: LineSegment StartX=-3.53088 StartY=-2.85015 StartZ=0 EndX=-3.46422 EndY=-2.68348 EndZ=0
    g226: LineSegment StartX=-3.46422 StartY=-2.68348 StartZ=0 EndX=-3.43088 EndY=-2.51681 EndZ=0
    g227: LineSegment StartX=-3.43088 StartY=-2.51681 StartZ=0 EndX=-3.43088 EndY=-2.31681 EndZ=0
    g228: LineSegment StartX=-3.43088 StartY=-2.31681 StartZ=0 EndX=-3.46422 EndY=-2.18348 EndZ=0
    g229: LineSegment StartX=-3.46422 StartY=-2.18348 StartZ=0 EndX=-3.63088 EndY=-1.91681 EndZ=0
    g230: LineSegment StartX=-3.63088 StartY=-1.91681 StartZ=0 EndX=-3.89755 EndY=-1.71681 EndZ=0
    g231: LineSegment StartX=-3.89755 StartY=-1.71681 StartZ=0 EndX=-4.19755 EndY=-1.65015 EndZ=0
    g232: LineSegment StartX=-4.19755 StartY=-1.65015 StartZ=0 EndX=-4.33088 EndY=-1.65015 EndZ=0
    g233: LineSegment StartX=-4.33088 StartY=-1.65015 StartZ=0 EndX=-4.53088 EndY=-1.71681 EndZ=0
    g234: LineSegment StartX=-4.53088 StartY=-1.71681 StartZ=0 EndX=-4.79755 EndY=-1.91681 EndZ=0
    g235: LineSegment StartX=-4.79755 StartY=-1.91681 StartZ=0 EndX=-4.96422 EndY=-2.18348 EndZ=0
    g236: LineSegment StartX=-4.96422 StartY=-2.18348 StartZ=0 EndX=-4.99755 EndY=-2.51681 EndZ=0
    g237: LineSegment StartX=-4.99755 StartY=-2.51681 StartZ=0 EndX=-4.89755 EndY=-2.85015 EndZ=0
    g238: LineSegment StartX=-4.89755 StartY=-2.85015 StartZ=0 EndX=-4.66422 EndY=-3.08348 EndZ=0
    g239: LineSegment StartX=-4.66422 StartY=-3.08348 StartZ=0 EndX=-4.49755 EndY=-3.15015 EndZ=0
    g240: LineSegment StartX=-4.49755 StartY=-3.15015 StartZ=0 EndX=-4.36422 EndY=-3.21681 EndZ=0
    g241: LineSegment StartX=-4.36422 StartY=-3.21681 StartZ=0 EndX=-4.19755 EndY=-3.25015 EndZ=0
    g242: LineSegment StartX=-4.19755 StartY=-3.25015 StartZ=0 EndX=-3.96422 EndY=-3.18348 EndZ=0
    g243: LineSegment StartX=56.6691 StartY=-1.58348 StartZ=0 EndX=56.8358 EndY=-1.55015 EndZ=0
    g244: LineSegment StartX=56.8358 StartY=-1.55015 StartZ=0 EndX=57.0691 EndY=-1.45015 EndZ=0
    g245: LineSegment StartX=57.0691 StartY=-1.45015 StartZ=0 EndX=57.2025 EndY=-1.31681 EndZ=0
    g246: LineSegment StartX=57.2025 StartY=-1.31681 StartZ=0 EndX=57.3691 EndY=-1.18348 EndZ=0
    g247: LineSegment StartX=57.3691 StartY=-1.18348 StartZ=0 EndX=57.4691 EndY=-0.850146 EndZ=0
    g248: LineSegment StartX=57.4691 StartY=-0.850146 StartZ=0 EndX=57.4358 EndY=-0.516813 EndZ=0
    g249: LineSegment StartX=57.4358 StartY=-0.516813 StartZ=0 EndX=57.3691 EndY=-0.416813 EndZ=0
    g250: LineSegment StartX=57.3691 StartY=-0.416813 StartZ=0 EndX=57.2691 EndY=-0.250146 EndZ=0
    g251: LineSegment StartX=57.2691 StartY=-0.250146 StartZ=0 EndX=57.0025 EndY=-0.0834796 EndZ=0
    g252: LineSegment StartX=57.0025 StartY=-0.0834796 StartZ=0 EndX=56.9025 EndY=-0.016813 EndZ=0
    g253: LineSegment StartX=56.9025 StartY=-0.016813 StartZ=0 EndX=56.6691 EndY=0.0165204 EndZ=0
    g254: LineSegment StartX=56.6691 StartY=0.0165204 StartZ=0 EndX=56.5025 EndY=-0.016813 EndZ=0
    g255: LineSegment StartX=56.5025 StartY=-0.016813 StartZ=0 EndX=56.3025 EndY=-0.0834796 EndZ=0
    g256: LineSegment StartX=56.3025 StartY=-0.0834796 StartZ=0 EndX=56.2025 EndY=-0.150146 EndZ=0
    g257: LineSegment StartX=56.2025 StartY=-0.150146 StartZ=0 EndX=56.0691 EndY=-0.250146 EndZ=0
    g258: LineSegment StartX=56.0691 StartY=-0.250146 StartZ=0 EndX=55.9691 EndY=-0.416813 EndZ=0
    g259: LineSegment StartX=55.9691 StartY=-0.416813 StartZ=0 EndX=55.9025 EndY=-0.516813 EndZ=0
    g260: LineSegment StartX=55.9025 StartY=-0.516813 StartZ=0 EndX=55.8691 EndY=-0.88348 EndZ=0
    g261: LineSegment StartX=55.8691 StartY=-0.88348 StartZ=0 EndX=55.9691 EndY=-1.18348 EndZ=0
    g262: LineSegment StartX=55.9691 StartY=-1.18348 StartZ=0 EndX=56.2691 EndY=-1.45015 EndZ=0
    g263: LineSegment StartX=56.2691 StartY=-1.45015 StartZ=0 EndX=56.5025 EndY=-1.55015 EndZ=0
    g264: LineSegment StartX=56.5025 StartY=-1.55015 StartZ=0 EndX=56.6691 EndY=-1.58348 EndZ=0
    g265: LineSegment StartX=2.23578 StartY=-4.01681 StartZ=0 EndX=2.06912 EndY=-3.91681 EndZ=0
    g266: LineSegment StartX=2.06912 StartY=-3.91681 StartZ=0 EndX=1.96912 EndY=-3.85015 EndZ=0
    g267: LineSegment StartX=1.96912 StartY=-3.85015 StartZ=0 EndX=1.63578 EndY=-3.78348 EndZ=0
    g268: LineSegment StartX=1.63578 StartY=-3.78348 StartZ=0 EndX=1.30245 EndY=-3.85015 EndZ=0
    g269: LineSegment StartX=1.30245 StartY=-3.85015 StartZ=0 EndX=1.03578 EndY=-4.01681 EndZ=0
    g270: LineSegment StartX=1.03578 StartY=-4.01681 StartZ=0 EndX=0.902451 EndY=-4.28348 EndZ=0
    g271: LineSegment StartX=0.902451 StartY=-4.28348 StartZ=0 EndX=0.835784 EndY=-4.65015 EndZ=0
    g272: LineSegment StartX=0.835784 StartY=-4.65015 StartZ=0 EndX=0.935784 EndY=-4.95015 EndZ=0
    g273: LineSegment StartX=0.935784 StartY=-4.95015 StartZ=0 EndX=1.00245 EndY=-5.05015 EndZ=0
    g274: LineSegment StartX=1.00245 StartY=-5.05015 StartZ=0 EndX=1.10245 EndY=-5.08348 EndZ=0
    g275: LineSegment StartX=1.10245 StartY=-5.08348 StartZ=0 EndX=1.16912 EndY=-5.21681 EndZ=0
    g276: LineSegment StartX=1.16912 StartY=-5.21681 StartZ=0 EndX=1.46912 EndY=-5.35015 EndZ=0
    g277: LineSegment StartX=1.46912 StartY=-5.35015 StartZ=0 EndX=1.56912 EndY=-5.35015 EndZ=0
    g278: LineSegment StartX=1.56912 StartY=-5.35015 StartZ=0 EndX=1.66912 EndY=-5.35015 EndZ=0
    g279: LineSegment StartX=1.66912 StartY=-5.35015 StartZ=0 EndX=1.80245 EndY=-5.35015 EndZ=0
    g280: LineSegment StartX=1.80245 StartY=-5.35015 StartZ=0 EndX=1.93578 EndY=-5.28348 EndZ=0
    g281: LineSegment StartX=1.93578 StartY=-5.28348 StartZ=0 EndX=2.10245 EndY=-5.21681 EndZ=0
    g282: LineSegment StartX=2.10245 StartY=-5.21681 StartZ=0 EndX=2.33578 EndY=-4.95015 EndZ=0
    g283: LineSegment StartX=2.33578 StartY=-4.95015 StartZ=0 EndX=2.43578 EndY=-4.65015 EndZ=0
    g284: LineSegment StartX=2.43578 StartY=-4.65015 StartZ=0 EndX=2.40245 EndY=-4.31681 EndZ=0
    g285: LineSegment StartX=2.40245 StartY=-4.31681 StartZ=0 EndX=2.30245 EndY=-4.15015 EndZ=0
    g286: LineSegment StartX=2.30245 StartY=-4.15015 StartZ=0 EndX=2.23578 EndY=-4.01681 EndZ=0
    g287: LineSegment StartX=2.76912 StartY=4.41652 StartZ=0 EndX=2.60245 EndY=4.31652 EndZ=0
    g288: LineSegment StartX=2.60245 StartY=4.31652 StartZ=0 EndX=2.50245 EndY=4.21652 EndZ=0
    g289: LineSegment StartX=2.50245 StartY=4.21652 StartZ=0 EndX=2.33578 EndY=3.94985 EndZ=0
    g290: LineSegment StartX=2.33578 StartY=3.94985 StartZ=0 EndX=2.30245 EndY=3.78319 EndZ=0
    g291: LineSegment StartX=2.30245 StartY=3.78319 StartZ=0 EndX=2.30245 EndY=3.64985 EndZ=0
    g292: LineSegment StartX=2.30245 StartY=3.64985 StartZ=0 EndX=2.40245 EndY=3.31652 EndZ=0
    g293: LineSegment StartX=2.40245 StartY=3.31652 StartZ=0 EndX=2.63578 EndY=3.04985 EndZ=0
    g294: LineSegment StartX=2.63578 StartY=3.04985 StartZ=0 EndX=2.76912 EndY=2.98319 EndZ=0
    g295: LineSegment StartX=2.76912 StartY=2.98319 StartZ=0 EndX=2.93578 EndY=2.91652 EndZ=0
    g296: LineSegment StartX=2.93578 StartY=2.91652 StartZ=0 EndX=3.10245 EndY=2.88319 EndZ=0
    g297: LineSegment StartX=3.10245 StartY=2.88319 StartZ=0 EndX=3.26912 EndY=2.91652 EndZ=0
    g298: LineSegment StartX=3.26912 StartY=2.91652 StartZ=0 EndX=3.43578 EndY=2.98319 EndZ=0
    g299: LineSegment StartX=3.43578 StartY=2.98319 StartZ=0 EndX=3.56912 EndY=3.04985 EndZ=0
    g300: LineSegment StartX=3.56912 StartY=3.04985 StartZ=0 EndX=3.80245 EndY=3.28319 EndZ=0
    g301: LineSegment StartX=3.80245 StartY=3.28319 StartZ=0 EndX=3.90245 EndY=3.61652 EndZ=0
    g302: LineSegment StartX=3.90245 StartY=3.61652 StartZ=0 EndX=3.86912 EndY=3.74985 EndZ=0
    g303: LineSegment StartX=3.86912 StartY=3.74985 StartZ=0 EndX=3.86912 EndY=3.94985 EndZ=0
    g304: LineSegment StartX=3.86912 StartY=3.94985 StartZ=0 EndX=3.70245 EndY=4.21652 EndZ=0
    g305: LineSegment StartX=3.70245 StartY=4.21652 StartZ=0 EndX=3.43578 EndY=4.41652 EndZ=0
    g306: LineSegment StartX=3.43578 StartY=4.41652 StartZ=0 EndX=3.10245 EndY=4.48319 EndZ=0
    g307: LineSegment StartX=3.10245 StartY=4.48319 StartZ=0 EndX=2.93578 EndY=4.44985 EndZ=0
    g308: LineSegment StartX=2.93578 StartY=4.44985 StartZ=0 EndX=2.76912 EndY=4.41652 EndZ=0
    g309: LineSegment StartX=4.00245 StartY=-1.68348 StartZ=0 EndX=3.83578 EndY=-1.71681 EndZ=0
    g310: LineSegment StartX=3.83578 StartY=-1.71681 StartZ=0 EndX=3.56912 EndY=-1.91681 EndZ=0
    g311: LineSegment StartX=3.56912 StartY=-1.91681 StartZ=0 EndX=3.46912 EndY=-2.08348 EndZ=0
    g312: LineSegment StartX=3.46912 StartY=-2.08348 StartZ=0 EndX=3.40245 EndY=-2.18348 EndZ=0
    g313: LineSegment StartX=3.40245 StartY=-2.18348 StartZ=0 EndX=3.36912 EndY=-2.51681 EndZ=0
    g314: LineSegment StartX=3.36912 StartY=-2.51681 StartZ=0 EndX=3.46912 EndY=-2.85015 EndZ=0
    g315: LineSegment StartX=3.46912 StartY=-2.85015 StartZ=0 EndX=3.56912 EndY=-2.95015 EndZ=0
    g316: LineSegment StartX=3.56912 StartY=-2.95015 StartZ=0 EndX=3.70245 EndY=-3.08348 EndZ=0
    g317: LineSegment StartX=3.70245 StartY=-3.08348 StartZ=0 EndX=4.00245 EndY=-3.21681 EndZ=0
    g318: LineSegment StartX=4.00245 StartY=-3.21681 StartZ=0 EndX=4.16912 EndY=-3.25015 EndZ=0
    g319: LineSegment StartX=4.16912 StartY=-3.25015 StartZ=0 EndX=4.33578 EndY=-3.21681 EndZ=0
    g320: LineSegment StartX=4.33578 StartY=-3.21681 StartZ=0 EndX=4.63578 EndY=-3.08348 EndZ=0
    g321: LineSegment StartX=4.63578 StartY=-3.08348 StartZ=0 EndX=4.86912 EndY=-2.85015 EndZ=0
    g322: LineSegment StartX=4.86912 StartY=-2.85015 StartZ=0 EndX=4.96912 EndY=-2.51681 EndZ=0
    g323: LineSegment StartX=4.96912 StartY=-2.51681 StartZ=0 EndX=4.93578 EndY=-2.18348 EndZ=0
    g324: LineSegment StartX=4.93578 StartY=-2.18348 StartZ=0 EndX=4.76912 EndY=-1.91681 EndZ=0
    g325: LineSegment StartX=4.76912 StartY=-1.91681 StartZ=0 EndX=4.50245 EndY=-1.71681 EndZ=0
    g326: LineSegment StartX=4.50245 StartY=-1.71681 StartZ=0 EndX=4.16912 EndY=-1.65015 EndZ=0
    g327: LineSegment StartX=4.16912 StartY=-1.65015 StartZ=0 EndX=4.00245 EndY=-1.68348 EndZ=0
    g328: LineSegment StartX=-4.33088 StartY=0.183187 StartZ=0 EndX=-4.09755 EndY=0.41652 EndZ=0
    g329: LineSegment StartX=-4.09755 StartY=0.41652 StartZ=0 EndX=-3.99755 EndY=0.749854 EndZ=0
    g330: LineSegment StartX=-3.99755 StartY=0.749854 StartZ=0 EndX=-4.03088 EndY=1.08319 EndZ=0
    g331: LineSegment StartX=-4.03088 StartY=1.08319 StartZ=0 EndX=-4.19755 EndY=1.34985 EndZ=0
    g332: LineSegment StartX=-4.19755 StartY=1.34985 StartZ=0 EndX=-4.46422 EndY=1.54985 EndZ=0
    g333: LineSegment StartX=-4.46422 StartY=1.54985 StartZ=0 EndX=-4.79755 EndY=1.61652 EndZ=0
    g334: LineSegment StartX=-4.79755 StartY=1.61652 StartZ=0 EndX=-4.89755 EndY=1.58319 EndZ=0
    g335: LineSegment StartX=-4.89755 StartY=1.58319 StartZ=0 EndX=-5.09755 EndY=1.54985 EndZ=0
    g336: LineSegment StartX=-5.09755 StartY=1.54985 StartZ=0 EndX=-5.36422 EndY=1.34985 EndZ=0
    g337: LineSegment StartX=-5.36422 StartY=1.34985 StartZ=0 EndX=-5.53088 EndY=1.08319 EndZ=0
    g338: LineSegment StartX=-5.53088 StartY=1.08319 StartZ=0 EndX=-5.56422 EndY=0.91652 EndZ=0
    g339: LineSegment StartX=-5.56422 StartY=0.91652 StartZ=0 EndX=-5.56422 EndY=0.749854 EndZ=0
    g340: LineSegment StartX=-5.56422 StartY=0.749854 StartZ=0 EndX=-5.46422 EndY=0.41652 EndZ=0
    g341: LineSegment StartX=-5.46422 StartY=0.41652 StartZ=0 EndX=-5.26422 EndY=0.183187 EndZ=0
    g342: LineSegment StartX=-5.26422 StartY=0.183187 StartZ=0 EndX=-4.96422 EndY=0.0498537 EndZ=0
    g343: LineSegment StartX=-4.96422 StartY=0.0498537 StartZ=0 EndX=-4.79755 EndY=0.0165204 EndZ=0
    g344: LineSegment StartX=-4.79755 StartY=0.0165204 StartZ=0 EndX=-4.63088 EndY=0.0498537 EndZ=0
    g345: LineSegment StartX=-4.63088 StartY=0.0498537 StartZ=0 EndX=-4.33088 EndY=0.183187 EndZ=0
    g346: LineSegment StartX=63.8025 StartY=-0.18348 StartZ=0 EndX=63.6358 EndY=-0.0501463 EndZ=0
    g347: LineSegment StartX=63.6358 StartY=-0.0501463 StartZ=0 EndX=63.5025 EndY=-0.016813 EndZ=0
    g348: LineSegment StartX=63.5025 StartY=-0.016813 StartZ=0 EndX=63.2691 EndY=0.0165204 EndZ=0
    g349: LineSegment StartX=63.2691 StartY=0.0165204 StartZ=0 EndX=63.0358 EndY=-0.016813 EndZ=0
    g350: LineSegment StartX=63.0358 StartY=-0.016813 StartZ=0 EndX=62.7025 EndY=-0.250146 EndZ=0
    g351: LineSegment StartX=62.7025 StartY=-0.250146 StartZ=0 EndX=62.5358 EndY=-0.516813 EndZ=0
    g352: LineSegment StartX=62.5358 StartY=-0.516813 StartZ=0 EndX=62.5025 EndY=-0.78348 EndZ=0
    g353: LineSegment StartX=62.5025 StartY=-0.78348 StartZ=0 EndX=62.6025 EndY=-1.18348 EndZ=0
    g354: LineSegment StartX=62.6025 StartY=-1.18348 StartZ=0 EndX=62.7025 EndY=-1.28348 EndZ=0
    g355: LineSegment StartX=62.7025 StartY=-1.28348 StartZ=0 EndX=62.8025 EndY=-1.31681 EndZ=0
    g356: LineSegment StartX=62.8025 StartY=-1.31681 StartZ=0 EndX=62.8691 EndY=-1.45015 EndZ=0
    g357: LineSegment StartX=62.8691 StartY=-1.45015 StartZ=0 EndX=63.0358 EndY=-1.51681 EndZ=0
    g358: LineSegment StartX=63.0358 StartY=-1.51681 StartZ=0 EndX=63.1691 EndY=-1.55015 EndZ=0
    g359: LineSegment StartX=63.1691 StartY=-1.55015 StartZ=0 EndX=63.3691 EndY=-1.58348 EndZ=0
    g360: LineSegment StartX=63.3691 StartY=-1.58348 StartZ=0 EndX=63.5025 EndY=-1.55015 EndZ=0
    g361: LineSegment StartX=63.5025 StartY=-1.55015 StartZ=0 EndX=63.7691 EndY=-1.41681 EndZ=0
    g362: LineSegment StartX=63.7691 StartY=-1.41681 StartZ=0 EndX=63.8691 EndY=-1.31681 EndZ=0
    g363: LineSegment StartX=63.8691 StartY=-1.31681 StartZ=0 EndX=64.0025 EndY=-1.18348 EndZ=0
    g364: LineSegment StartX=64.0025 StartY=-1.18348 StartZ=0 EndX=64.1025 EndY=-0.850146 EndZ=0
    g365: LineSegment StartX=64.1025 StartY=-0.850146 StartZ=0 EndX=64.0691 EndY=-0.516813 EndZ=0
    g366: LineSegment StartX=64.0691 StartY=-0.516813 StartZ=0 EndX=63.9691 EndY=-0.350146 EndZ=0
    g367: LineSegment StartX=63.9691 StartY=-0.350146 StartZ=0 EndX=63.9025 EndY=-0.250146 EndZ=0
    g368: LineSegment StartX=63.9025 StartY=-0.250146 StartZ=0 EndX=63.8025 EndY=-0.18348 EndZ=0
    g369: LineSegment StartX=62.2358 StartY=2.78319 StartZ=0 EndX=62.0691 EndY=2.64985 EndZ=0
    g370: LineSegment StartX=62.0691 StartY=2.64985 StartZ=0 EndX=61.9691 EndY=2.51652 EndZ=0
    g371: LineSegment StartX=61.9691 StartY=2.51652 StartZ=0 EndX=61.8691 EndY=2.28319 EndZ=0
    g372: LineSegment StartX=61.8691 StartY=2.28319 StartZ=0 EndX=61.8358 EndY=2.01652 EndZ=0
    g373: LineSegment StartX=61.8358 StartY=2.01652 StartZ=0 EndX=61.9691 EndY=1.71652 EndZ=0
    g374: LineSegment StartX=61.9691 StartY=1.71652 StartZ=0 EndX=62.1691 EndY=1.48319 EndZ=0
    g375: LineSegment StartX=62.1691 StartY=1.48319 StartZ=0 EndX=62.3691 EndY=1.38319 EndZ=0
    g376: LineSegment StartX=62.3691 StartY=1.38319 StartZ=0 EndX=62.4691 EndY=1.31652 EndZ=0
    g377: LineSegment StartX=62.4691 StartY=1.31652 StartZ=0 EndX=62.6358 EndY=1.31652 EndZ=0
    g378: LineSegment StartX=62.6358 StartY=1.31652 StartZ=0 EndX=62.7358 EndY=1.31652 EndZ=0
    g379: LineSegment StartX=62.7358 StartY=1.31652 StartZ=0 EndX=62.8358 EndY=1.34985 EndZ=0
    g380: LineSegment StartX=62.8358 StartY=1.34985 StartZ=0 EndX=62.9358 EndY=1.38319 EndZ=0
    g381: LineSegment StartX=62.9358 StartY=1.38319 StartZ=0 EndX=63.0358 EndY=1.41652 EndZ=0
    g382: LineSegment StartX=63.0358 StartY=1.41652 StartZ=0 EndX=63.1358 EndY=1.48319 EndZ=0
    g383: LineSegment StartX=63.1358 StartY=1.48319 StartZ=0 EndX=63.1691 EndY=1.58319 EndZ=0
    g384: LineSegment StartX=63.1691 StartY=1.58319 StartZ=0 EndX=63.3358 EndY=1.71652 EndZ=0
    g385: LineSegment StartX=63.3358 StartY=1.71652 StartZ=0 EndX=63.4025 EndY=1.88319 EndZ=0
    g386: LineSegment StartX=63.4025 StartY=1.88319 StartZ=0 EndX=63.4358 EndY=2.01652 EndZ=0
    g387: LineSegment StartX=63.4358 StartY=2.01652 StartZ=0 EndX=63.4025 EndY=2.34985 EndZ=0
    g388: LineSegment StartX=63.4025 StartY=2.34985 StartZ=0 EndX=63.2025 EndY=2.68319 EndZ=0
    g389: LineSegment StartX=63.2025 StartY=2.68319 StartZ=0 EndX=62.9691 EndY=2.84985 EndZ=0
    g390: LineSegment StartX=62.9691 StartY=2.84985 StartZ=0 EndX=62.6358 EndY=2.91652 EndZ=0
    g391: LineSegment StartX=62.6358 StartY=2.91652 StartZ=0 EndX=62.3691 EndY=2.84985 EndZ=0
    g392: LineSegment StartX=62.3691 StartY=2.84985 StartZ=0 EndX=62.2358 EndY=2.78319 EndZ=0
FEATURE [Part::Feature] ReferenceFrame002
  Placement = pos=(0,0,9.99) rot=(0,0,1;0rad)
FEATURE [PartDesign::Plane] DatumPlane_upperArm_3
  Length = 20
  Placement = pos=(0,0,9.99) rot=(0,0,1;0rad)
  ResizeMode = 0
  Width = 20
FEATURE [Sketcher::SketchObject] SVGSketch_upperArm_3
  FullyConstrained = false
  Placement = pos=(0,0,9.99) rot=(0,0,1;0rad)
  sketch-geometry (164):
    g0: LineSegment StartX=58.0434 StartY=-4.61333 StartZ=0 EndX=58.3634 EndY=-4.74667 EndZ=0
    g1: LineSegment StartX=58.3634 StartY=-4.74667 StartZ=0 EndX=58.8434 EndY=-4.85333 EndZ=0
    g2: LineSegment StartX=58.8434 StartY=-4.85333 StartZ=0 EndX=59.1634 EndY=-4.93333 EndZ=0
    g3: LineSegment StartX=59.1634 StartY=-4.93333 StartZ=0 EndX=59.9901 EndY=-5.01333 EndZ=0
    g4: LineSegment StartX=59.9901 StartY=-5.01333 StartZ=0 EndX=60.0701 EndY=-5.01333 EndZ=0
    g5: LineSegment StartX=60.0701 StartY=-5.01333 StartZ=0 EndX=60.8168 EndY=-4.93333 EndZ=0
    g6: LineSegment StartX=60.8168 StartY=-4.93333 StartZ=0 EndX=61.1101 EndY=-4.88 EndZ=0
    g7: LineSegment StartX=61.1101 StartY=-4.88 StartZ=0 EndX=61.1901 EndY=-4.85333 EndZ=0
    g8: LineSegment StartX=61.1901 StartY=-4.85333 StartZ=0 EndX=61.6168 EndY=-4.74667 EndZ=0
    g9: LineSegment StartX=61.6168 StartY=-4.74667 StartZ=0 EndX=61.8834 EndY=-4.64 EndZ=0
    g10: LineSegment StartX=61.8834 StartY=-4.64 StartZ=0 EndX=62.0968 EndY=-4.53333 EndZ=0
    g11: LineSegment StartX=62.0968 StartY=-4.53333 StartZ=0 EndX=62.3634 EndY=-4.4 EndZ=0
    g12: LineSegment StartX=62.3634 StartY=-4.4 StartZ=0 EndX=62.5234 EndY=-4.32 EndZ=0
    g13: LineSegment StartX=62.5234 StartY=-4.32 StartZ=0 EndX=63.0568 EndY=-3.94667 EndZ=0
    g14: LineSegment StartX=63.0568 StartY=-3.94667 StartZ=0 EndX=63.1901 EndY=-3.84 EndZ=0
    g15: LineSegment StartX=63.1901 StartY=-3.84 StartZ=0 EndX=63.6701 EndY=-3.38667 EndZ=0
    g16: LineSegment StartX=63.6701 StartY=-3.38667 StartZ=0 EndX=63.7234 EndY=-3.30667 EndZ=0
    g17: LineSegment StartX=63.7234 StartY=-3.30667 StartZ=0 EndX=64.1768 EndY=-2.74667 EndZ=0
    g18: LineSegment StartX=64.1768 StartY=-2.74667 StartZ=0 EndX=64.3634 EndY=-2.42667 EndZ=0
    g19: LineSegment StartX=64.3634 StartY=-2.42667 StartZ=0 EndX=64.5768 EndY=-2.02667 EndZ=0
    g20: LineSegment StartX=64.5768 StartY=-2.02667 StartZ=0 EndX=64.6034 EndY=-1.92 EndZ=0
    g21: LineSegment StartX=64.6034 StartY=-1.92 StartZ=0 EndX=64.7368 EndY=-1.54667 EndZ=0
    g22: LineSegment StartX=64.7368 StartY=-1.54667 StartZ=0 EndX=64.7634 EndY=-1.46667 EndZ=0
    g23: LineSegment StartX=64.7634 StartY=-1.46667 StartZ=0 EndX=64.8434 EndY=-1.25333 EndZ=0
    g24: LineSegment StartX=64.8434 StartY=-1.25333 StartZ=0 EndX=64.8968 EndY=-0.8 EndZ=0
    g25: LineSegment StartX=64.8968 StartY=-0.8 StartZ=0 EndX=64.9768 EndY=-0.426667 EndZ=0
    g26: LineSegment StartX=64.9768 StartY=-0.426667 StartZ=0 EndX=64.9768 EndY=-0.08 EndZ=0
    g27: LineSegment StartX=64.9768 StartY=-0.08 StartZ=0 EndX=64.9768 EndY=0.4 EndZ=0
    g28: LineSegment StartX=64.9768 StartY=0.4 StartZ=0 EndX=64.9234 EndY=0.666667 EndZ=0
    g29: LineSegment StartX=64.9234 StartY=0.666667 StartZ=0 EndX=64.8434 EndY=1.22667 EndZ=0
    g30: LineSegment StartX=64.8434 StartY=1.22667 StartZ=0 EndX=64.6834 EndY=1.62667 EndZ=0
    g31: LineSegment StartX=64.6834 StartY=1.62667 StartZ=0 EndX=64.5768 EndY=2 EndZ=0
    g32: LineSegment StartX=64.5768 StartY=2 StartZ=0 EndX=64.2568 EndY=2.56 EndZ=0
    g33: LineSegment StartX=64.2568 StartY=2.56 StartZ=0 EndX=64.1768 EndY=2.72 EndZ=0
    g34: LineSegment StartX=64.1768 StartY=2.72 StartZ=0 EndX=63.7768 EndY=3.22667 EndZ=0
    g35: LineSegment StartX=63.7768 StartY=3.22667 StartZ=0 EndX=63.6701 EndY=3.36 EndZ=0
    g36: LineSegment StartX=63.6701 StartY=3.36 StartZ=0 EndX=63.4568 EndY=3.54667 EndZ=0
    g37: LineSegment StartX=63.4568 StartY=3.54667 StartZ=0 EndX=63.2968 EndY=3.70667 EndZ=0
    g38: LineSegment StartX=63.2968 StartY=3.70667 StartZ=0 EndX=63.0568 EndY=3.92 EndZ=0
    g39: LineSegment StartX=63.0568 StartY=3.92 StartZ=0 EndX=62.3634 EndY=4.37333 EndZ=0
    g40: LineSegment StartX=62.3634 StartY=4.37333 StartZ=0 EndX=61.6168 EndY=4.72 EndZ=0
    g41: LineSegment StartX=61.6168 StartY=4.72 StartZ=0 EndX=60.8168 EndY=4.90667 EndZ=0
    g42: LineSegment StartX=60.8168 StartY=4.90667 StartZ=0 EndX=59.9901 EndY=4.98667 EndZ=0
    g43: LineSegment StartX=59.9901 StartY=4.98667 StartZ=0 EndX=59.1634 EndY=4.90667 EndZ=0
    g44: LineSegment StartX=59.1634 StartY=4.90667 StartZ=0 EndX=58.8434 EndY=4.82667 EndZ=0
    g45: LineSegment StartX=58.8434 StartY=4.82667 StartZ=0 EndX=58.3634 EndY=4.72 EndZ=0
    g46: LineSegment StartX=58.3634 StartY=4.72 StartZ=0 EndX=57.6168 EndY=4.37333 EndZ=0
    g47: LineSegment StartX=57.6168 StartY=4.37333 StartZ=0 EndX=56.9234 EndY=3.92 EndZ=0
    g48: LineSegment StartX=56.9234 StartY=3.92 StartZ=0 EndX=56.4968 EndY=3.54667 EndZ=0
    g49: LineSegment StartX=56.4968 StartY=3.54667 StartZ=0 EndX=56.3101 EndY=3.36 EndZ=0
    g50: LineSegment StartX=56.3101 StartY=3.36 StartZ=0 EndX=56.2034 EndY=3.22667 EndZ=0
    g51: LineSegment StartX=56.2034 StartY=3.22667 StartZ=0 EndX=55.8834 EndY=2.77333 EndZ=0
    g52: LineSegment StartX=55.8834 StartY=2.77333 StartZ=0 EndX=55.8034 EndY=2.72 EndZ=0
    g53: LineSegment StartX=55.8034 StartY=2.72 StartZ=0 EndX=55.7501 EndY=2.61333 EndZ=0
    g54: LineSegment StartX=55.7501 StartY=2.61333 StartZ=0 EndX=55.6968 EndY=2.48 EndZ=0
    g55: LineSegment StartX=55.6968 StartY=2.48 StartZ=0 EndX=55.4034 EndY=2 EndZ=0
    g56: LineSegment StartX=55.4034 StartY=2 StartZ=0 EndX=55.3234 EndY=1.73333 EndZ=0
    g57: LineSegment StartX=55.3234 StartY=1.73333 StartZ=0 EndX=55.1368 EndY=1.22667 EndZ=0
    g58: LineSegment StartX=55.1368 StartY=1.22667 StartZ=0 EndX=55.1368 EndY=1.12 EndZ=0
    g59: LineSegment StartX=55.1368 StartY=1.12 StartZ=0 EndX=55.0568 EndY=0.666667 EndZ=0
    g60: LineSegment StartX=55.0568 StartY=0.666667 StartZ=0 EndX=55.0034 EndY=0.4 EndZ=0
    g61: LineSegment StartX=55.0034 StartY=0.4 StartZ=0 EndX=55.0034 EndY=0.293333 EndZ=0
    g62: LineSegment StartX=55.0034 StartY=0.293333 StartZ=0 EndX=55.0034 EndY=0.213333 EndZ=0
    g63: LineSegment StartX=55.0034 StartY=0.213333 StartZ=0 EndX=55.0034 EndY=-0.426667 EndZ=0
    g64: LineSegment StartX=55.0034 StartY=-0.426667 StartZ=0 EndX=55.1101 EndY=-1.06667 EndZ=0
    g65: LineSegment StartX=55.1101 StartY=-1.06667 StartZ=0 EndX=55.1368 EndY=-1.17333 EndZ=0
    g66: LineSegment StartX=55.1368 StartY=-1.17333 StartZ=0 EndX=55.1368 EndY=-1.25333 EndZ=0
    g67: LineSegment StartX=55.1368 StartY=-1.25333 StartZ=0 EndX=55.2168 EndY=-1.44 EndZ=0
    g68: LineSegment StartX=55.2168 StartY=-1.44 StartZ=0 EndX=55.2434 EndY=-1.54667 EndZ=0
    g69: LineSegment StartX=55.2434 StartY=-1.54667 StartZ=0 EndX=55.3768 EndY=-1.92 EndZ=0
    g70: LineSegment StartX=55.3768 StartY=-1.92 StartZ=0 EndX=55.4034 EndY=-2.02667 EndZ=0
    g71: LineSegment StartX=55.4034 StartY=-2.02667 StartZ=0 EndX=55.8034 EndY=-2.74667 EndZ=0
    g72: LineSegment StartX=55.8034 StartY=-2.74667 StartZ=0 EndX=56.0968 EndY=-3.12 EndZ=0
    g73: LineSegment StartX=56.0968 StartY=-3.12 StartZ=0 EndX=56.2034 EndY=-3.25333 EndZ=0
    g74: LineSegment StartX=56.2034 StartY=-3.25333 StartZ=0 EndX=56.3101 EndY=-3.38667 EndZ=0
    g75: LineSegment StartX=56.3101 StartY=-3.38667 StartZ=0 EndX=56.9234 EndY=-3.94667 EndZ=0
    g76: LineSegment StartX=56.9234 StartY=-3.94667 StartZ=0 EndX=57.0301 EndY=-4.02667 EndZ=0
    g77: LineSegment StartX=57.0301 StartY=-4.02667 StartZ=0 EndX=57.1368 EndY=-4.10667 EndZ=0
    g78: LineSegment StartX=57.1368 StartY=-4.10667 StartZ=0 EndX=57.6168 EndY=-4.4 EndZ=0
    g79: LineSegment StartX=57.6168 StartY=-4.4 StartZ=0 EndX=58.0434 EndY=-4.61333 EndZ=0
    g80: LineSegment StartX=-0.916554 StartY=5.92 StartZ=0 EndX=-1.76989 EndY=5.73333 EndZ=0
    g81: LineSegment StartX=-1.76989 StartY=5.73333 StartZ=0 EndX=-2.62322 EndY=5.38667 EndZ=0
    g82: LineSegment StartX=-2.62322 StartY=5.38667 StartZ=0 EndX=-2.96989 EndY=5.2 EndZ=0
    g83: LineSegment StartX=-2.96989 StartY=5.2 StartZ=0 EndX=-3.18322 EndY=5.06667 EndZ=0
    g84: LineSegment StartX=-3.18322 StartY=5.06667 StartZ=0 EndX=-3.39655 EndY=4.93333 EndZ=0
    g85: LineSegment StartX=-3.39655 StartY=4.93333 StartZ=0 EndX=-3.95655 EndY=4.50667 EndZ=0
    g86: LineSegment StartX=-3.95655 StartY=4.50667 StartZ=0 EndX=-4.08989 EndY=4.37333 EndZ=0
    g87: LineSegment StartX=-4.08989 StartY=4.37333 StartZ=0 EndX=-4.70322 EndY=3.73333 EndZ=0
    g88: LineSegment StartX=-4.70322 StartY=3.73333 StartZ=0 EndX=-5.10322 EndY=3.12 EndZ=0
    g89: LineSegment StartX=-5.10322 StartY=3.12 StartZ=0 EndX=-5.20989 EndY=2.98667 EndZ=0
    g90: LineSegment StartX=-5.20989 StartY=2.98667 StartZ=0 EndX=-5.26322 EndY=2.88 EndZ=0
    g91: LineSegment StartX=-5.26322 StartY=2.88 StartZ=0 EndX=-5.28989 EndY=2.8 EndZ=0
    g92: LineSegment StartX=-5.28989 StartY=2.8 StartZ=0 EndX=-5.34322 EndY=2.69333 EndZ=0
    g93: LineSegment StartX=-5.34322 StartY=2.69333 StartZ=0 EndX=-5.50322 EndY=2.4 EndZ=0
    g94: LineSegment StartX=-5.50322 StartY=2.4 StartZ=0 EndX=-5.60989 EndY=2.18667 EndZ=0
    g95: LineSegment StartX=-5.60989 StartY=2.18667 StartZ=0 EndX=-5.84989 EndY=1.33333 EndZ=0
    g96: LineSegment StartX=-5.84989 StartY=1.33333 StartZ=0 EndX=-5.87655 EndY=1.22667 EndZ=0
    g97: LineSegment StartX=-5.87655 StartY=1.22667 StartZ=0 EndX=-5.98322 EndY=0.426667 EndZ=0
    g98: LineSegment StartX=-5.98322 StartY=0.426667 StartZ=0 EndX=-5.98322 EndY=-0.0266667 EndZ=0
    g99: LineSegment StartX=-5.98322 StartY=-0.0266667 StartZ=0 EndX=-5.98322 EndY=-0.453333 EndZ=0
    g100: LineSegment StartX=-5.98322 StartY=-0.453333 StartZ=0 EndX=-5.95655 EndY=-0.8 EndZ=0
    g101: LineSegment StartX=-5.95655 StartY=-0.8 StartZ=0 EndX=-5.84989 EndY=-1.36 EndZ=0
    g102: LineSegment StartX=-5.84989 StartY=-1.36 StartZ=0 EndX=-5.60989 EndY=-2.21333 EndZ=0
    g103: LineSegment StartX=-5.60989 StartY=-2.21333 StartZ=0 EndX=-5.47655 EndY=-2.45333 EndZ=0
    g104: LineSegment StartX=-5.47655 StartY=-2.45333 StartZ=0 EndX=-5.28989 EndY=-2.88 EndZ=0
    g105: LineSegment StartX=-5.28989 StartY=-2.88 StartZ=0 EndX=-5.20989 EndY=-3.01333 EndZ=0
    g106: LineSegment StartX=-5.20989 StartY=-3.01333 StartZ=0 EndX=-4.88989 EndY=-3.49333 EndZ=0
    g107: LineSegment StartX=-4.88989 StartY=-3.49333 StartZ=0 EndX=-4.70322 EndY=-3.76 EndZ=0
    g108: LineSegment StartX=-4.70322 StartY=-3.76 StartZ=0 EndX=-4.08989 EndY=-4.4 EndZ=0
    g109: LineSegment StartX=-4.08989 StartY=-4.4 StartZ=0 EndX=-3.95655 EndY=-4.53333 EndZ=0
    g110: LineSegment StartX=-3.95655 StartY=-4.53333 StartZ=0 EndX=-3.39655 EndY=-4.96 EndZ=0
    g111: LineSegment StartX=-3.39655 StartY=-4.96 StartZ=0 EndX=-2.96989 EndY=-5.22667 EndZ=0
    g112: LineSegment StartX=-2.96989 StartY=-5.22667 StartZ=0 EndX=-2.70322 EndY=-5.36 EndZ=0
    g113: LineSegment StartX=-2.70322 StartY=-5.36 StartZ=0 EndX=-2.62322 EndY=-5.41333 EndZ=0
    g114: LineSegment StartX=-2.62322 StartY=-5.41333 StartZ=0 EndX=-1.76989 EndY=-5.76 EndZ=0
    g115: LineSegment StartX=-1.76989 StartY=-5.76 StartZ=0 EndX=-0.916554 EndY=-5.94667 EndZ=0
    g116: LineSegment StartX=-0.916554 StartY=-5.94667 StartZ=0 EndX=-0.836554 EndY=-5.94667 EndZ=0
    g117: LineSegment StartX=-0.836554 StartY=-5.94667 StartZ=0 EndX=-0.623221 EndY=-5.97333 EndZ=0
    g118: LineSegment StartX=-0.623221 StartY=-5.97333 StartZ=0 EndX=-0.00988772 EndY=-6 EndZ=0
    g119: LineSegment StartX=-0.00988772 StartY=-6 StartZ=0 EndX=0.603446 EndY=-5.97333 EndZ=0
    g120: LineSegment StartX=0.603446 StartY=-5.97333 StartZ=0 EndX=0.710112 EndY=-5.94667 EndZ=0
    g121: LineSegment StartX=0.710112 StartY=-5.94667 StartZ=0 EndX=0.816779 EndY=-5.94667 EndZ=0
    g122: LineSegment StartX=0.816779 StartY=-5.94667 StartZ=0 EndX=1.56345 EndY=-5.78667 EndZ=0
    g123: LineSegment StartX=1.56345 StartY=-5.78667 StartZ=0 EndX=1.75011 EndY=-5.73333 EndZ=0
    g124: LineSegment StartX=1.75011 StartY=-5.73333 StartZ=0 EndX=1.85678 EndY=-5.70667 EndZ=0
    g125: LineSegment StartX=1.85678 StartY=-5.70667 StartZ=0 EndX=2.39011 EndY=-5.49333 EndZ=0
    g126: LineSegment StartX=2.39011 StartY=-5.49333 StartZ=0 EndX=2.57678 EndY=-5.41333 EndZ=0
    g127: LineSegment StartX=2.57678 StartY=-5.41333 StartZ=0 EndX=2.68345 EndY=-5.36 EndZ=0
    g128: LineSegment StartX=2.68345 StartY=-5.36 StartZ=0 EndX=2.92345 EndY=-5.22667 EndZ=0
    g129: LineSegment StartX=2.92345 StartY=-5.22667 StartZ=0 EndX=3.37678 EndY=-4.96 EndZ=0
    g130: LineSegment StartX=3.37678 StartY=-4.96 StartZ=0 EndX=3.93678 EndY=-4.53333 EndZ=0
    g131: LineSegment StartX=3.93678 StartY=-4.53333 StartZ=0 EndX=4.07011 EndY=-4.4 EndZ=0
    g132: LineSegment StartX=4.07011 StartY=-4.4 StartZ=0 EndX=4.68345 EndY=-3.76 EndZ=0
    g133: LineSegment StartX=4.68345 StartY=-3.76 StartZ=0 EndX=4.84345 EndY=-3.49333 EndZ=0
    g134: LineSegment StartX=4.84345 StartY=-3.49333 StartZ=0 EndX=5.19011 EndY=-3.01333 EndZ=0
    g135: LineSegment StartX=5.19011 StartY=-3.01333 StartZ=0 EndX=5.24345 EndY=-2.88 EndZ=0
    g136: LineSegment StartX=5.24345 StartY=-2.88 StartZ=0 EndX=5.56345 EndY=-2.21333 EndZ=0
    g137: LineSegment StartX=5.56345 StartY=-2.21333 StartZ=0 EndX=5.72345 EndY=-1.65333 EndZ=0
    g138: LineSegment StartX=5.72345 StartY=-1.65333 StartZ=0 EndX=5.83011 EndY=-1.36 EndZ=0
    g139: LineSegment StartX=5.83011 StartY=-1.36 StartZ=0 EndX=5.85678 EndY=-1.25333 EndZ=0
    g140: LineSegment StartX=5.85678 StartY=-1.25333 StartZ=0 EndX=5.85678 EndY=-1.17333 EndZ=0
    g141: LineSegment StartX=5.85678 StartY=-1.17333 StartZ=0 EndX=5.91011 EndY=-0.8 EndZ=0
    g142: LineSegment StartX=5.91011 StartY=-0.8 StartZ=0 EndX=5.96345 EndY=-0.586667 EndZ=0
    g143: LineSegment StartX=5.96345 StartY=-0.586667 StartZ=0 EndX=5.96345 EndY=-0.453333 EndZ=0
    g144: LineSegment StartX=5.96345 StartY=-0.453333 StartZ=0 EndX=5.96345 EndY=0.426667 EndZ=0
    g145: LineSegment StartX=5.96345 StartY=0.426667 StartZ=0 EndX=5.83011 EndY=1.33333 EndZ=0
    g146: LineSegment StartX=5.83011 StartY=1.33333 StartZ=0 EndX=5.56345 EndY=2.18667 EndZ=0
    g147: LineSegment StartX=5.56345 StartY=2.18667 StartZ=0 EndX=5.32345 EndY=2.69333 EndZ=0
    g148: LineSegment StartX=5.32345 StartY=2.69333 StartZ=0 EndX=5.19011 EndY=2.98667 EndZ=0
    g149: LineSegment StartX=5.19011 StartY=2.98667 StartZ=0 EndX=5.08345 EndY=3.12 EndZ=0
    g150: LineSegment StartX=5.08345 StartY=3.12 StartZ=0 EndX=4.68345 EndY=3.73333 EndZ=0
    g151: LineSegment StartX=4.68345 StartY=3.73333 StartZ=0 EndX=4.60345 EndY=3.81333 EndZ=0
    g152: LineSegment StartX=4.60345 StartY=3.81333 StartZ=0 EndX=4.07011 EndY=4.37333 EndZ=0
    g153: LineSegment StartX=4.07011 StartY=4.37333 StartZ=0 EndX=3.93678 EndY=4.50667 EndZ=0
    g154: LineSegment StartX=3.93678 StartY=4.50667 StartZ=0 EndX=3.37678 EndY=4.93333 EndZ=0
    g155: LineSegment StartX=3.37678 StartY=4.93333 StartZ=0 EndX=3.16345 EndY=5.06667 EndZ=0
    g156: LineSegment StartX=3.16345 StartY=5.06667 StartZ=0 EndX=2.92345 EndY=5.2 EndZ=0
    g157: LineSegment StartX=2.92345 StartY=5.2 StartZ=0 EndX=2.57678 EndY=5.38667 EndZ=0
    g158: LineSegment StartX=2.57678 StartY=5.38667 StartZ=0 EndX=1.75011 EndY=5.73333 EndZ=0
    g159: LineSegment StartX=1.75011 StartY=5.73333 StartZ=0 EndX=1.56345 EndY=5.76 EndZ=0
    g160: LineSegment StartX=1.56345 StartY=5.76 StartZ=0 EndX=0.870112 EndY=5.92 EndZ=0
    g161: LineSegment StartX=0.870112 StartY=5.92 StartZ=0 EndX=-0.00988772 EndY=6 EndZ=0
    g162: LineSegment StartX=-0.00988772 StartY=6 StartZ=0 EndX=-0.836554 EndY=5.92 EndZ=0
    g163: LineSegment StartX=-0.836554 StartY=5.92 StartZ=0 EndX=-0.916554 EndY=5.92 EndZ=0
FEATURE [Part::Feature] ReferenceFrame003
FEATURE [PartDesign::Plane] DatumPlane_upperArm_4
  Length = 20
  ResizeMode = 0
  Width = 20
FEATURE [Sketcher::SketchObject] SVGSketch_upperArm_4
  FullyConstrained = false
  sketch-geometry (232):
    g0: LineSegment StartX=62.5834 StartY=1.5 StartZ=0 EndX=62.6168 EndY=1.4 EndZ=0
    g1: LineSegment StartX=62.6168 StartY=1.4 StartZ=0 EndX=62.4168 EndY=1.73333 EndZ=0
    g2: LineSegment StartX=62.4168 StartY=1.73333 StartZ=0 EndX=62.3834 EndY=1.83333 EndZ=0
    g3: LineSegment StartX=62.3834 StartY=1.83333 StartZ=0 EndX=62.2168 EndY=2 EndZ=0
    g4: LineSegment StartX=62.2168 StartY=2 StartZ=0 EndX=62.0834 EndY=2.13333 EndZ=0
    g5: LineSegment StartX=62.0834 StartY=2.13333 StartZ=0 EndX=61.7501 EndY=2.4 EndZ=0
    g6: LineSegment StartX=61.7501 StartY=2.4 StartZ=0 EndX=61.4501 EndY=2.63333 EndZ=0
    g7: LineSegment StartX=61.4501 StartY=2.63333 StartZ=0 EndX=61.2168 EndY=2.73333 EndZ=0
    g8: LineSegment StartX=61.2168 StartY=2.73333 StartZ=0 EndX=61.0834 EndY=2.76667 EndZ=0
    g9: LineSegment StartX=61.0834 StartY=2.76667 StartZ=0 EndX=60.6168 EndY=2.93333 EndZ=0
    g10: LineSegment StartX=60.6168 StartY=2.93333 StartZ=0 EndX=59.9834 EndY=3 EndZ=0
    g11: LineSegment StartX=59.9834 StartY=3 StartZ=0 EndX=59.4501 EndY=2.93333 EndZ=0
    g12: LineSegment StartX=59.4501 StartY=2.93333 StartZ=0 EndX=59.3501 EndY=2.93333 EndZ=0
    g13: LineSegment StartX=59.3501 StartY=2.93333 StartZ=0 EndX=58.7501 EndY=2.73333 EndZ=0
    g14: LineSegment StartX=58.7501 StartY=2.73333 StartZ=0 EndX=58.2168 EndY=2.4 EndZ=0
    g15: LineSegment StartX=58.2168 StartY=2.4 StartZ=0 EndX=57.7501 EndY=2 EndZ=0
    g16: LineSegment StartX=57.7501 StartY=2 StartZ=0 EndX=57.3834 EndY=1.5 EndZ=0
    g17: LineSegment StartX=57.3834 StartY=1.5 StartZ=0 EndX=57.1168 EndY=0.9 EndZ=0
    g18: LineSegment StartX=57.1168 StartY=0.9 StartZ=0 EndX=56.9834 EndY=0.3 EndZ=0
    g19: LineSegment StartX=56.9834 StartY=0.3 StartZ=0 EndX=56.9834 EndY=-0.333333 EndZ=0
    g20: LineSegment StartX=56.9834 StartY=-0.333333 StartZ=0 EndX=57.1168 EndY=-0.933333 EndZ=0
    g21: LineSegment StartX=57.1168 StartY=-0.933333 StartZ=0 EndX=57.3834 EndY=-1.53333 EndZ=0
    g22: LineSegment StartX=57.3834 StartY=-1.53333 StartZ=0 EndX=57.7501 EndY=-2.03333 EndZ=0
    g23: LineSegment StartX=57.7501 StartY=-2.03333 StartZ=0 EndX=58.0168 EndY=-2.3 EndZ=0
    g24: LineSegment StartX=58.0168 StartY=-2.3 StartZ=0 EndX=58.2168 EndY=-2.43333 EndZ=0
    g25: LineSegment StartX=58.2168 StartY=-2.43333 StartZ=0 EndX=58.3834 EndY=-2.56667 EndZ=0
    g26: LineSegment StartX=58.3834 StartY=-2.56667 StartZ=0 EndX=58.7501 EndY=-2.76667 EndZ=0
    g27: LineSegment StartX=58.7501 StartY=-2.76667 StartZ=0 EndX=59.3501 EndY=-2.96667 EndZ=0
    g28: LineSegment StartX=59.3501 StartY=-2.96667 StartZ=0 EndX=59.4834 EndY=-2.96667 EndZ=0
    g29: LineSegment StartX=59.4834 StartY=-2.96667 StartZ=0 EndX=59.8834 EndY=-3 EndZ=0
    g30: LineSegment StartX=59.8834 StartY=-3 StartZ=0 EndX=59.9834 EndY=-3 EndZ=0
    g31: LineSegment StartX=59.9834 StartY=-3 StartZ=0 EndX=60.2834 EndY=-3 EndZ=0
    g32: LineSegment StartX=60.2834 StartY=-3 StartZ=0 EndX=60.3834 EndY=-3 EndZ=0
    g33: LineSegment StartX=60.3834 StartY=-3 StartZ=0 EndX=60.6168 EndY=-2.96667 EndZ=0
    g34: LineSegment StartX=60.6168 StartY=-2.96667 StartZ=0 EndX=60.7168 EndY=-2.9 EndZ=0
    g35: LineSegment StartX=60.7168 StartY=-2.9 StartZ=0 EndX=61.2168 EndY=-2.76667 EndZ=0
    g36: LineSegment StartX=61.2168 StartY=-2.76667 StartZ=0 EndX=61.7501 EndY=-2.43333 EndZ=0
    g37: LineSegment StartX=61.7501 StartY=-2.43333 StartZ=0 EndX=62.0501 EndY=-2.23333 EndZ=0
    g38: LineSegment StartX=62.0501 StartY=-2.23333 StartZ=0 EndX=62.2168 EndY=-2.03333 EndZ=0
    g39: LineSegment StartX=62.2168 StartY=-2.03333 StartZ=0 EndX=62.5834 EndY=-1.53333 EndZ=0
    g40: LineSegment StartX=62.5834 StartY=-1.53333 StartZ=0 EndX=62.8501 EndY=-0.933333 EndZ=0
    g41: LineSegment StartX=62.8501 StartY=-0.933333 StartZ=0 EndX=62.8834 EndY=-0.666667 EndZ=0
    g42: LineSegment StartX=62.8834 StartY=-0.666667 StartZ=0 EndX=62.9834 EndY=-0.333333 EndZ=0
    g43: LineSegment StartX=62.9834 StartY=-0.333333 StartZ=0 EndX=62.9834 EndY=0.2 EndZ=0
    g44: LineSegment StartX=62.9834 StartY=0.2 StartZ=0 EndX=62.9834 EndY=0.3 EndZ=0
    g45: LineSegment StartX=62.9834 StartY=0.3 StartZ=0 EndX=62.9168 EndY=0.7 EndZ=0
    g46: LineSegment StartX=62.9168 StartY=0.7 StartZ=0 EndX=62.8501 EndY=0.9 EndZ=0
    g47: LineSegment StartX=62.8501 StartY=0.9 StartZ=0 EndX=62.7834 EndY=1 EndZ=0
    g48: LineSegment StartX=62.7834 StartY=1 StartZ=0 EndX=62.5834 EndY=1.5 EndZ=0
    g49: LineSegment StartX=-0.0165544 StartY=3 StartZ=0 EndX=-0.549888 EndY=2.93333 EndZ=0
    g50: LineSegment StartX=-0.549888 StartY=2.93333 StartZ=0 EndX=-0.649888 EndY=2.93333 EndZ=0
    g51: LineSegment StartX=-0.649888 StartY=2.93333 StartZ=0 EndX=-1.24989 EndY=2.73333 EndZ=0
    g52: LineSegment StartX=-1.24989 StartY=2.73333 StartZ=0 EndX=-1.78322 EndY=2.4 EndZ=0
    g53: LineSegment StartX=-1.78322 StartY=2.4 StartZ=0 EndX=-2.24989 EndY=2 EndZ=0
    g54: LineSegment StartX=-2.24989 StartY=2 StartZ=0 EndX=-2.61655 EndY=1.5 EndZ=0
    g55: LineSegment StartX=-2.61655 StartY=1.5 StartZ=0 EndX=-2.88322 EndY=0.9 EndZ=0
    g56: LineSegment StartX=-2.88322 StartY=0.9 StartZ=0 EndX=-3.01655 EndY=0.3 EndZ=0
    g57: LineSegment StartX=-3.01655 StartY=0.3 StartZ=0 EndX=-3.01655 EndY=-0.333333 EndZ=0
    g58: LineSegment StartX=-3.01655 StartY=-0.333333 StartZ=0 EndX=-2.88322 EndY=-0.933333 EndZ=0
    g59: LineSegment StartX=-2.88322 StartY=-0.933333 StartZ=0 EndX=-2.61655 EndY=-1.53333 EndZ=0
    g60: LineSegment StartX=-2.61655 StartY=-1.53333 StartZ=0 EndX=-2.24989 EndY=-2.03333 EndZ=0
    g61: LineSegment StartX=-2.24989 StartY=-2.03333 StartZ=0 EndX=-1.98322 EndY=-2.3 EndZ=0
    g62: LineSegment StartX=-1.98322 StartY=-2.3 StartZ=0 EndX=-1.78322 EndY=-2.43333 EndZ=0
    g63: LineSegment StartX=-1.78322 StartY=-2.43333 StartZ=0 EndX=-1.61655 EndY=-2.56667 EndZ=0
    g64: LineSegment StartX=-1.61655 StartY=-2.56667 StartZ=0 EndX=-1.24989 EndY=-2.76667 EndZ=0
    g65: LineSegment StartX=-1.24989 StartY=-2.76667 StartZ=0 EndX=-0.649888 EndY=-2.96667 EndZ=0
    g66: LineSegment StartX=-0.649888 StartY=-2.96667 StartZ=0 EndX=-0.516554 EndY=-2.96667 EndZ=0
    g67: LineSegment StartX=-0.516554 StartY=-2.96667 StartZ=0 EndX=-0.116554 EndY=-3 EndZ=0
    g68: LineSegment StartX=-0.116554 StartY=-3 StartZ=0 EndX=-0.0165544 EndY=-3 EndZ=0
    g69: LineSegment StartX=-0.0165544 StartY=-3 StartZ=0 EndX=0.283446 EndY=-3 EndZ=0
    g70: LineSegment StartX=0.283446 StartY=-3 StartZ=0 EndX=0.383446 EndY=-3 EndZ=0
    g71: LineSegment StartX=0.383446 StartY=-3 StartZ=0 EndX=0.616779 EndY=-2.96667 EndZ=0
    g72: LineSegment StartX=0.616779 StartY=-2.96667 StartZ=0 EndX=0.716779 EndY=-2.9 EndZ=0
    g73: LineSegment StartX=0.716779 StartY=-2.9 StartZ=0 EndX=1.21678 EndY=-2.76667 EndZ=0
    g74: LineSegment StartX=1.21678 StartY=-2.76667 StartZ=0 EndX=1.75011 EndY=-2.43333 EndZ=0
    g75: LineSegment StartX=1.75011 StartY=-2.43333 StartZ=0 EndX=2.05011 EndY=-2.23333 EndZ=0
    g76: LineSegment StartX=2.05011 StartY=-2.23333 StartZ=0 EndX=2.21678 EndY=-2.03333 EndZ=0
    g77: LineSegment StartX=2.21678 StartY=-2.03333 StartZ=0 EndX=2.58345 EndY=-1.53333 EndZ=0
    g78: LineSegment StartX=2.58345 StartY=-1.53333 StartZ=0 EndX=2.85011 EndY=-0.933333 EndZ=0
    g79: LineSegment StartX=2.85011 StartY=-0.933333 StartZ=0 EndX=2.88345 EndY=-0.666667 EndZ=0
    g80: LineSegment StartX=2.88345 StartY=-0.666667 StartZ=0 EndX=2.98345 EndY=-0.333333 EndZ=0
    g81: LineSegment StartX=2.98345 StartY=-0.333333 StartZ=0 EndX=2.98345 EndY=0.2 EndZ=0
    g82: LineSegment StartX=2.98345 StartY=0.2 StartZ=0 EndX=2.98345 EndY=0.3 EndZ=0
    g83: LineSegment StartX=2.98345 StartY=0.3 StartZ=0 EndX=2.85011 EndY=0.9 EndZ=0
    g84: LineSegment StartX=2.85011 StartY=0.9 StartZ=0 EndX=2.78345 EndY=1 EndZ=0
    g85: LineSegment StartX=2.78345 StartY=1 StartZ=0 EndX=2.61678 EndY=1.4 EndZ=0
    g86: LineSegment StartX=2.61678 StartY=1.4 StartZ=0 EndX=2.58345 EndY=1.5 EndZ=0
    g87: LineSegment StartX=2.58345 StartY=1.5 StartZ=0 EndX=2.41678 EndY=1.73333 EndZ=0
    g88: LineSegment StartX=2.41678 StartY=1.73333 StartZ=0 EndX=2.38345 EndY=1.83333 EndZ=0
    g89: LineSegment StartX=2.38345 StartY=1.83333 StartZ=0 EndX=2.21678 EndY=2 EndZ=0
    g90: LineSegment StartX=2.21678 StartY=2 StartZ=0 EndX=2.08345 EndY=2.13333 EndZ=0
    g91: LineSegment StartX=2.08345 StartY=2.13333 StartZ=0 EndX=1.75011 EndY=2.4 EndZ=0
    g92: LineSegment StartX=1.75011 StartY=2.4 StartZ=0 EndX=1.45011 EndY=2.63333 EndZ=0
    g93: LineSegment StartX=1.45011 StartY=2.63333 StartZ=0 EndX=1.21678 EndY=2.73333 EndZ=0
    g94: LineSegment StartX=1.21678 StartY=2.73333 StartZ=0 EndX=1.08345 EndY=2.76667 EndZ=0
    g95: LineSegment StartX=1.08345 StartY=2.76667 StartZ=0 EndX=0.616779 EndY=2.93333 EndZ=0
    g96: LineSegment StartX=0.616779 StartY=2.93333 StartZ=0 EndX=0.316779 EndY=2.93333 EndZ=0
    g97: LineSegment StartX=0.316779 StartY=2.93333 StartZ=0 EndX=-0.0165544 EndY=3 EndZ=0
    g98: LineSegment StartX=59.1501 StartY=-4.93333 StartZ=0 EndX=59.9834 EndY=-5 EndZ=0
    g99: LineSegment StartX=59.9834 StartY=-5 StartZ=0 EndX=60.8168 EndY=-4.93333 EndZ=0
    g100: LineSegment StartX=60.8168 StartY=-4.93333 StartZ=0 EndX=61.0834 EndY=-4.86667 EndZ=0
    g101: LineSegment StartX=61.0834 StartY=-4.86667 StartZ=0 EndX=61.6168 EndY=-4.73333 EndZ=0
    g102: LineSegment StartX=61.6168 StartY=-4.73333 StartZ=0 EndX=61.8834 EndY=-4.63333 EndZ=0
    g103: LineSegment StartX=61.8834 StartY=-4.63333 StartZ=0 EndX=62.0834 EndY=-4.53333 EndZ=0
    g104: LineSegment StartX=62.0834 StartY=-4.53333 StartZ=0 EndX=62.3501 EndY=-4.4 EndZ=0
    g105: LineSegment StartX=62.3501 StartY=-4.4 StartZ=0 EndX=62.5168 EndY=-4.3 EndZ=0
    g106: LineSegment StartX=62.5168 StartY=-4.3 StartZ=0 EndX=63.0501 EndY=-3.96667 EndZ=0
    g107: LineSegment StartX=63.0501 StartY=-3.96667 StartZ=0 EndX=63.6501 EndY=-3.4 EndZ=0
    g108: LineSegment StartX=63.6501 StartY=-3.4 StartZ=0 EndX=63.7501 EndY=-3.3 EndZ=0
    g109: LineSegment StartX=63.7501 StartY=-3.3 StartZ=0 EndX=64.1834 EndY=-2.76667 EndZ=0
    g110: LineSegment StartX=64.1834 StartY=-2.76667 StartZ=0 EndX=64.3168 EndY=-2.43333 EndZ=0
    g111: LineSegment StartX=64.3168 StartY=-2.43333 StartZ=0 EndX=64.5501 EndY=-2.03333 EndZ=0
    g112: LineSegment StartX=64.5501 StartY=-2.03333 StartZ=0 EndX=64.7501 EndY=-1.53333 EndZ=0
    g113: LineSegment StartX=64.7501 StartY=-1.53333 StartZ=0 EndX=64.8168 EndY=-1.23333 EndZ=0
    g114: LineSegment StartX=64.8168 StartY=-1.23333 StartZ=0 EndX=64.9168 EndY=-0.8 EndZ=0
    g115: LineSegment StartX=64.9168 StartY=-0.8 StartZ=0 EndX=64.9501 EndY=-0.433333 EndZ=0
    g116: LineSegment StartX=64.9501 StartY=-0.433333 StartZ=0 EndX=64.9501 EndY=-0.0666667 EndZ=0
    g117: LineSegment StartX=64.9501 StartY=-0.0666667 StartZ=0 EndX=64.9501 EndY=0.4 EndZ=0
    g118: LineSegment StartX=64.9501 StartY=0.4 StartZ=0 EndX=64.8168 EndY=1.2 EndZ=0
    g119: LineSegment StartX=64.8168 StartY=1.2 StartZ=0 EndX=64.7168 EndY=1.6 EndZ=0
    g120: LineSegment StartX=64.7168 StartY=1.6 StartZ=0 EndX=64.5501 EndY=2 EndZ=0
    g121: LineSegment StartX=64.5501 StartY=2 StartZ=0 EndX=64.2834 EndY=2.53333 EndZ=0
    g122: LineSegment StartX=64.2834 StartY=2.53333 StartZ=0 EndX=64.1834 EndY=2.73333 EndZ=0
    g123: LineSegment StartX=64.1834 StartY=2.73333 StartZ=0 EndX=63.7834 EndY=3.23333 EndZ=0
    g124: LineSegment StartX=63.7834 StartY=3.23333 StartZ=0 EndX=63.6501 EndY=3.36667 EndZ=0
    g125: LineSegment StartX=63.6501 StartY=3.36667 StartZ=0 EndX=63.2834 EndY=3.7 EndZ=0
    g126: LineSegment StartX=63.2834 StartY=3.7 StartZ=0 EndX=63.0501 EndY=3.93333 EndZ=0
    g127: LineSegment StartX=63.0501 StartY=3.93333 StartZ=0 EndX=62.3501 EndY=4.36667 EndZ=0
    g128: LineSegment StartX=62.3501 StartY=4.36667 StartZ=0 EndX=61.6168 EndY=4.7 EndZ=0
    g129: LineSegment StartX=61.6168 StartY=4.7 StartZ=0 EndX=60.8168 EndY=4.9 EndZ=0
    g130: LineSegment StartX=60.8168 StartY=4.9 StartZ=0 EndX=59.9834 EndY=5 EndZ=0
    g131: LineSegment StartX=59.9834 StartY=5 StartZ=0 EndX=59.1501 EndY=4.9 EndZ=0
    g132: LineSegment StartX=59.1501 StartY=4.9 StartZ=0 EndX=58.3501 EndY=4.7 EndZ=0
    g133: LineSegment StartX=58.3501 StartY=4.7 StartZ=0 EndX=57.6168 EndY=4.36667 EndZ=0
    g134: LineSegment StartX=57.6168 StartY=4.36667 StartZ=0 EndX=56.9168 EndY=3.93333 EndZ=0
    g135: LineSegment StartX=56.9168 StartY=3.93333 StartZ=0 EndX=56.3168 EndY=3.36667 EndZ=0
    g136: LineSegment StartX=56.3168 StartY=3.36667 StartZ=0 EndX=56.2168 EndY=3.26667 EndZ=0
    g137: LineSegment StartX=56.2168 StartY=3.26667 StartZ=0 EndX=56.0834 EndY=3.06667 EndZ=0
    g138: LineSegment StartX=56.0834 StartY=3.06667 StartZ=0 EndX=55.7834 EndY=2.73333 EndZ=0
    g139: LineSegment StartX=55.7834 StartY=2.73333 StartZ=0 EndX=55.4168 EndY=2 EndZ=0
    g140: LineSegment StartX=55.4168 StartY=2 StartZ=0 EndX=55.2168 EndY=1.46667 EndZ=0
    g141: LineSegment StartX=55.2168 StartY=1.46667 StartZ=0 EndX=55.1501 EndY=1.2 EndZ=0
    g142: LineSegment StartX=55.1501 StartY=1.2 StartZ=0 EndX=55.1168 EndY=1.1 EndZ=0
    g143: LineSegment StartX=55.1168 StartY=1.1 StartZ=0 EndX=55.0834 EndY=1 EndZ=0
    g144: LineSegment StartX=55.0834 StartY=1 StartZ=0 EndX=45.2834 EndY=1 EndZ=0
    g145: LineSegment StartX=45.2834 StartY=1 StartZ=0 EndX=29.4501 EndY=1 EndZ=0
    g146: LineSegment StartX=29.4501 StartY=1 StartZ=0 EndX=9.11678 EndY=1 EndZ=0
    g147: LineSegment StartX=9.11678 StartY=1 StartZ=0 EndX=6.28345 EndY=0.966667 EndZ=0
    g148: LineSegment StartX=6.28345 StartY=0.966667 StartZ=0 EndX=5.95011 EndY=0.966667 EndZ=0
    g149: LineSegment StartX=5.95011 StartY=0.966667 StartZ=0 EndX=5.85011 EndY=1.2 EndZ=0
    g150: LineSegment StartX=5.85011 StartY=1.2 StartZ=0 EndX=5.81678 EndY=1.33333 EndZ=0
    g151: LineSegment StartX=5.81678 StartY=1.33333 StartZ=0 EndX=5.61678 EndY=2 EndZ=0
    g152: LineSegment StartX=5.61678 StartY=2 StartZ=0 EndX=5.58345 EndY=2.16667 EndZ=0
    g153: LineSegment StartX=5.58345 StartY=2.16667 StartZ=0 EndX=5.45011 EndY=2.4 EndZ=0
    g154: LineSegment StartX=5.45011 StartY=2.4 StartZ=0 EndX=5.18345 EndY=3 EndZ=0
    g155: LineSegment StartX=5.18345 StartY=3 StartZ=0 EndX=5.08345 EndY=3.13333 EndZ=0
    g156: LineSegment StartX=5.08345 StartY=3.13333 StartZ=0 EndX=4.68345 EndY=3.73333 EndZ=0
    g157: LineSegment StartX=4.68345 StartY=3.73333 StartZ=0 EndX=4.58345 EndY=3.8 EndZ=0
    g158: LineSegment StartX=4.58345 StartY=3.8 StartZ=0 EndX=4.05011 EndY=4.36667 EndZ=0
    g159: LineSegment StartX=4.05011 StartY=4.36667 StartZ=0 EndX=3.35011 EndY=4.93333 EndZ=0
    g160: LineSegment StartX=3.35011 StartY=4.93333 StartZ=0 EndX=2.58345 EndY=5.4 EndZ=0
    g161: LineSegment StartX=2.58345 StartY=5.4 StartZ=0 EndX=1.75011 EndY=5.73333 EndZ=0
    g162: LineSegment StartX=1.75011 StartY=5.73333 StartZ=0 EndX=0.883446 EndY=5.9 EndZ=0
    g163: LineSegment StartX=0.883446 StartY=5.9 StartZ=0 EndX=-0.0165544 EndY=5.96667 EndZ=0
    g164: LineSegment StartX=-0.0165544 StartY=5.96667 StartZ=0 EndX=-0.916554 EndY=5.9 EndZ=0
    g165: LineSegment StartX=-0.916554 StartY=5.9 StartZ=0 EndX=-1.78322 EndY=5.73333 EndZ=0
    g166: LineSegment StartX=-1.78322 StartY=5.73333 StartZ=0 EndX=-2.61655 EndY=5.4 EndZ=0
    g167: LineSegment StartX=-2.61655 StartY=5.4 StartZ=0 EndX=-3.38322 EndY=4.93333 EndZ=0
    g168: LineSegment StartX=-3.38322 StartY=4.93333 StartZ=0 EndX=-4.08322 EndY=4.36667 EndZ=0
    g169: LineSegment StartX=-4.08322 StartY=4.36667 StartZ=0 EndX=-4.71655 EndY=3.73333 EndZ=0
    g170: LineSegment StartX=-4.71655 StartY=3.73333 StartZ=0 EndX=-5.11655 EndY=3.13333 EndZ=0
    g171: LineSegment StartX=-5.11655 StartY=3.13333 StartZ=0 EndX=-5.21655 EndY=3 EndZ=0
    g172: LineSegment StartX=-5.21655 StartY=3 StartZ=0 EndX=-5.48322 EndY=2.43333 EndZ=0
    g173: LineSegment StartX=-5.48322 StartY=2.43333 StartZ=0 EndX=-5.61655 EndY=2.16667 EndZ=0
    g174: LineSegment StartX=-5.61655 StartY=2.16667 StartZ=0 EndX=-5.84989 EndY=1.33333 EndZ=0
    g175: LineSegment StartX=-5.84989 StartY=1.33333 StartZ=0 EndX=-5.88322 EndY=1.23333 EndZ=0
    g176: LineSegment StartX=-5.88322 StartY=1.23333 StartZ=0 EndX=-5.98322 EndY=0.433333 EndZ=0
    g177: LineSegment StartX=-5.98322 StartY=0.433333 StartZ=0 EndX=-5.98322 EndY=0.333333 EndZ=0
    g178: LineSegment StartX=-5.98322 StartY=0.333333 StartZ=0 EndX=-5.98322 EndY=0 EndZ=0
    g179: LineSegment StartX=-5.98322 StartY=0 StartZ=0 EndX=-5.98322 EndY=-0.466667 EndZ=0
    g180: LineSegment StartX=-5.98322 StartY=-0.466667 StartZ=0 EndX=-5.84989 EndY=-1.36667 EndZ=0
    g181: LineSegment StartX=-5.84989 StartY=-1.36667 StartZ=0 EndX=-5.61655 EndY=-2.2 EndZ=0
    g182: LineSegment StartX=-5.61655 StartY=-2.2 StartZ=0 EndX=-5.48322 EndY=-2.43333 EndZ=0
    g183: LineSegment StartX=-5.48322 StartY=-2.43333 StartZ=0 EndX=-5.21655 EndY=-3 EndZ=0
    g184: LineSegment StartX=-5.21655 StartY=-3 StartZ=0 EndX=-4.84989 EndY=-3.53333 EndZ=0
    g185: LineSegment StartX=-4.84989 StartY=-3.53333 StartZ=0 EndX=-4.71655 EndY=-3.76667 EndZ=0
    g186: LineSegment StartX=-4.71655 StartY=-3.76667 StartZ=0 EndX=-4.08322 EndY=-4.4 EndZ=0
    g187: LineSegment StartX=-4.08322 StartY=-4.4 StartZ=0 EndX=-3.38322 EndY=-4.96667 EndZ=0
    g188: LineSegment StartX=-3.38322 StartY=-4.96667 StartZ=0 EndX=-3.01655 EndY=-5.2 EndZ=0
    g189: LineSegment StartX=-3.01655 StartY=-5.2 StartZ=0 EndX=-2.61655 EndY=-5.43333 EndZ=0
    g190: LineSegment StartX=-2.61655 StartY=-5.43333 StartZ=0 EndX=-1.78322 EndY=-5.76667 EndZ=0
    g191: LineSegment StartX=-1.78322 StartY=-5.76667 StartZ=0 EndX=-0.916554 EndY=-5.93333 EndZ=0
    g192: LineSegment StartX=-0.916554 StartY=-5.93333 StartZ=0 EndX=-0.649888 EndY=-5.96667 EndZ=0
    g193: LineSegment StartX=-0.649888 StartY=-5.96667 StartZ=0 EndX=-0.0165544 EndY=-6 EndZ=0
    g194: LineSegment StartX=-0.0165544 StartY=-6 StartZ=0 EndX=0.583446 EndY=-5.96667 EndZ=0
    g195: LineSegment StartX=0.583446 StartY=-5.96667 StartZ=0 EndX=0.683446 EndY=-5.96667 EndZ=0
    g196: LineSegment StartX=0.683446 StartY=-5.96667 StartZ=0 EndX=0.883446 EndY=-5.93333 EndZ=0
    g197: LineSegment StartX=0.883446 StartY=-5.93333 StartZ=0 EndX=1.58345 EndY=-5.8 EndZ=0
    g198: LineSegment StartX=1.58345 StartY=-5.8 StartZ=0 EndX=1.75011 EndY=-5.76667 EndZ=0
    g199: LineSegment StartX=1.75011 StartY=-5.76667 StartZ=0 EndX=2.38345 EndY=-5.5 EndZ=0
    g200: LineSegment StartX=2.38345 StartY=-5.5 StartZ=0 EndX=2.58345 EndY=-5.43333 EndZ=0
    g201: LineSegment StartX=2.58345 StartY=-5.43333 StartZ=0 EndX=2.98345 EndY=-5.2 EndZ=0
    g202: LineSegment StartX=2.98345 StartY=-5.2 StartZ=0 EndX=3.15011 EndY=-5.1 EndZ=0
    g203: LineSegment StartX=3.15011 StartY=-5.1 StartZ=0 EndX=3.35011 EndY=-4.96667 EndZ=0
    g204: LineSegment StartX=3.35011 StartY=-4.96667 StartZ=0 EndX=3.85011 EndY=-4.6 EndZ=0
    g205: LineSegment StartX=3.85011 StartY=-4.6 StartZ=0 EndX=4.05011 EndY=-4.4 EndZ=0
    g206: LineSegment StartX=4.05011 StartY=-4.4 StartZ=0 EndX=4.18345 EndY=-4.26667 EndZ=0
    g207: LineSegment StartX=4.18345 StartY=-4.26667 StartZ=0 EndX=4.68345 EndY=-3.76667 EndZ=0
    g208: LineSegment StartX=4.68345 StartY=-3.76667 StartZ=0 EndX=4.81678 EndY=-3.53333 EndZ=0
    g209: LineSegment StartX=4.81678 StartY=-3.53333 StartZ=0 EndX=5.18345 EndY=-3 EndZ=0
    g210: LineSegment StartX=5.18345 StartY=-3 StartZ=0 EndX=5.41678 EndY=-2.5 EndZ=0
    g211: LineSegment StartX=5.41678 StartY=-2.5 StartZ=0 EndX=5.58345 EndY=-2.2 EndZ=0
    g212: LineSegment StartX=5.58345 StartY=-2.2 StartZ=0 EndX=5.75011 EndY=-1.66667 EndZ=0
    g213: LineSegment StartX=5.75011 StartY=-1.66667 StartZ=0 EndX=5.81678 EndY=-1.36667 EndZ=0
    g214: LineSegment StartX=5.81678 StartY=-1.36667 StartZ=0 EndX=5.85011 EndY=-1.26667 EndZ=0
    g215: LineSegment StartX=5.85011 StartY=-1.26667 StartZ=0 EndX=5.88345 EndY=-1.03333 EndZ=0
    g216: LineSegment StartX=5.88345 StartY=-1.03333 StartZ=0 EndX=36.2168 EndY=-1.03333 EndZ=0
    g217: LineSegment StartX=36.2168 StartY=-1.03333 StartZ=0 EndX=49.8501 EndY=-1 EndZ=0
    g218: LineSegment StartX=49.8501 StartY=-1 StartZ=0 EndX=54.6168 EndY=-1 EndZ=0
    g219: LineSegment StartX=54.6168 StartY=-1 StartZ=0 EndX=55.0501 EndY=-1 EndZ=0
    g220: LineSegment StartX=55.0501 StartY=-1 StartZ=0 EndX=55.1501 EndY=-1.23333 EndZ=0
    g221: LineSegment StartX=55.1501 StartY=-1.23333 StartZ=0 EndX=55.4168 EndY=-2.03333 EndZ=0
    g222: LineSegment StartX=55.4168 StartY=-2.03333 StartZ=0 EndX=55.6834 EndY=-2.56667 EndZ=0
    g223: LineSegment StartX=55.6834 StartY=-2.56667 StartZ=0 EndX=55.7834 EndY=-2.76667 EndZ=0
    g224: LineSegment StartX=55.7834 StartY=-2.76667 StartZ=0 EndX=56.3168 EndY=-3.4 EndZ=0
    g225: LineSegment StartX=56.3168 StartY=-3.4 StartZ=0 EndX=56.9168 EndY=-3.96667 EndZ=0
    g226: LineSegment StartX=56.9168 StartY=-3.96667 StartZ=0 EndX=57.0168 EndY=-4.03333 EndZ=0
    g227: LineSegment StartX=57.0168 StartY=-4.03333 StartZ=0 EndX=57.1168 EndY=-4.1 EndZ=0
    g228: LineSegment StartX=57.1168 StartY=-4.1 StartZ=0 EndX=57.6168 EndY=-4.4 EndZ=0
    g229: LineSegment StartX=57.6168 StartY=-4.4 StartZ=0 EndX=58.0168 EndY=-4.6 EndZ=0
    g230: LineSegment StartX=58.0168 StartY=-4.6 StartZ=0 EndX=58.3501 EndY=-4.73333 EndZ=0
    g231: LineSegment StartX=58.3501 StartY=-4.73333 StartZ=0 EndX=59.1501 EndY=-4.93333 EndZ=0
FEATURE [PartDesign::Body] upperArm_body
  AllowCompound = false
  Group = -> [DatumPlane_upperArm_1,SVGSketch_upperArm_1,DatumPlane_upperArm_2,SVGSketch_upperArm_2,DatumPlane_upperArm_3,SVGSketch_upperArm_3,DatumPlane_upperArm_4,SVGSketch_upperArm_4]
  Origin = -> Origin
FEATURE [Mesh::Feature] upperArm_Mesh
FEATURE [Mesh::Feature] TheCube_Mesh
